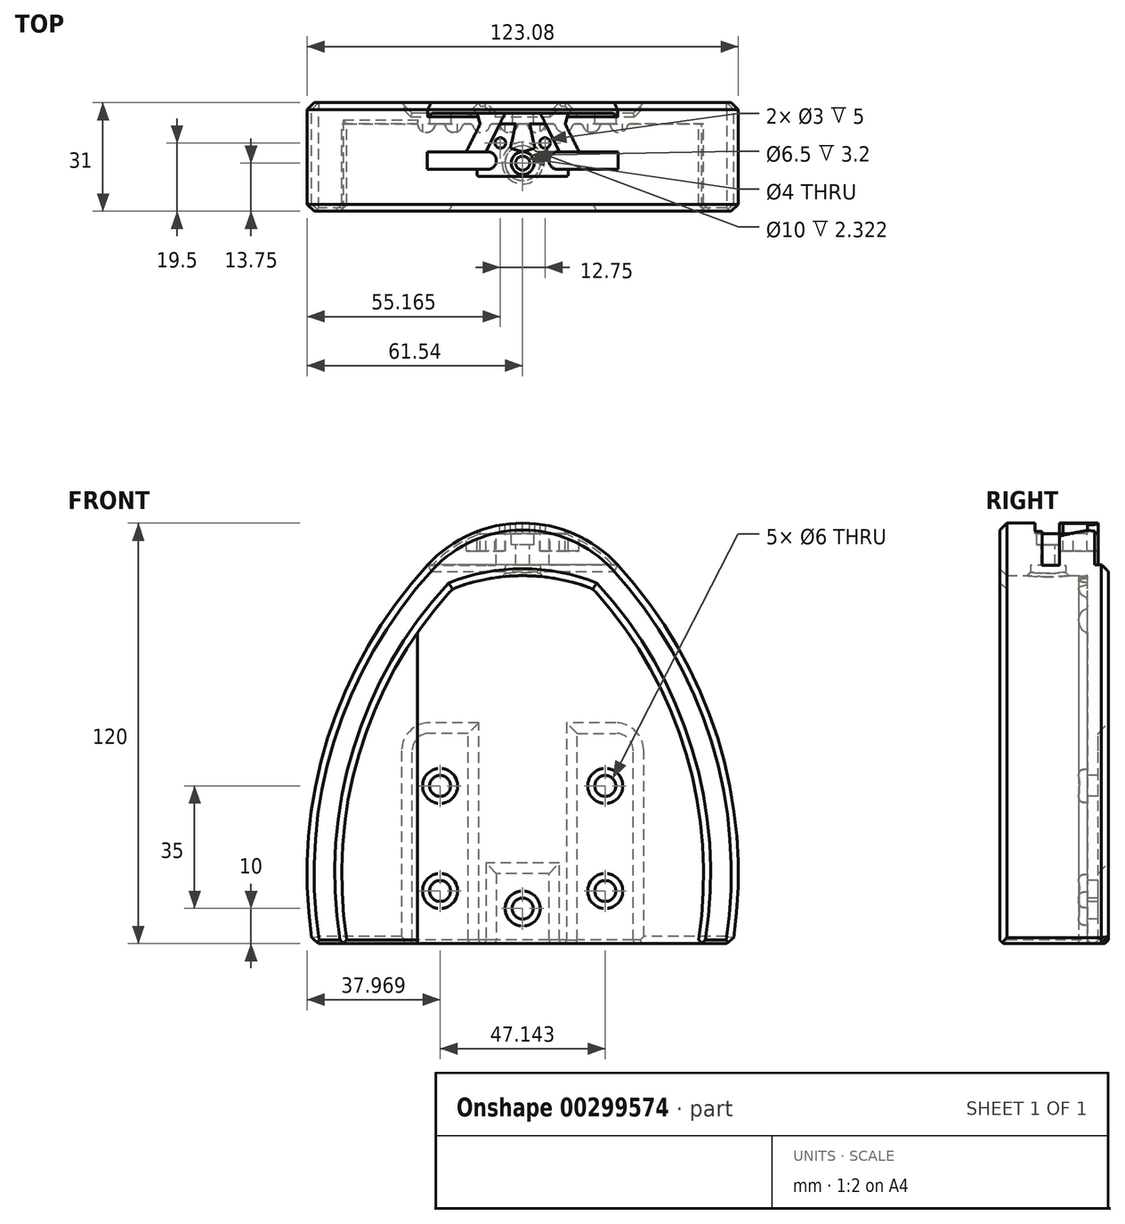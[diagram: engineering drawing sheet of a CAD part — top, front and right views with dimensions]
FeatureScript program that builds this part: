
annotation { "Feature Type Name" : "Feature", "Feature Type Description" : "" }
export const myFeature = defineFeature(function(context is Context, id is Id, definition is map)
    precondition{}
    {
        {
            assignVariable(context, id + "F0", {"name" : "LHeel", "anyValue" : 120 * mm});
        }
        {
            assignVariable(context, id + "F1", {"name" : "THeel", "anyValue" : 15 * mm});
        }
        {
            var Q0;
            Q0=qCreatedBy(makeId("Front.planeOp"),FACE);
            var sketch = newSketch(context, id + "F2", { "sketchPlane" : qUnion([Q0])});
            skArc(sketch, "E0", {"start": v(0, 120) * mm, "mid": v(-14.77, 116.9) * mm, "end": v(-27.05, 108.16) * mm});
            skArc(sketch, "E1", {"start": v(-27.05, 108.16) * mm, "mid": v(-55.9, 57.85) * mm, "end": v(-60, 0) * mm});
            skLineSegment(sketch, "E2", {"start": v(-60, 0) * mm, "end": v(0, 0) * mm});
            skArc(sketch, "E3.MirrorCS", {"start": v(0, 120) * mm, "mid": v(14.77, 116.9) * mm, "end": v(27.05, 108.16) * mm});
            skArc(sketch, "E4.MirrorCS", {"start": v(27.05, 108.16) * mm, "mid": v(55.9, 57.85) * mm, "end": v(60, 0) * mm});
            skLineSegment(sketch, "E5.MirrorCS", {"start": v(60, 0) * mm, "end": v(0, 0) * mm});
            skSolve(sketch);
        }
        {
            var Q0;
            Q0=makeQuery(id+"F2.imprint","IMPRINT",FACE,{"disambiguationData":[TD([[makeQuery(id+"F2.imprint","IMPRINT",EDGE,{"derivedFrom":sQuery(id+"F2.wireOp",EDGE,"E0")}),1.0]])]});
            extrude(context, id + "F3", {"entities" : qUnion([Q0]), "depth" : 3 * mm});
        }
        {
            var Q0;
            Q0=makeQuery(id+"F3.opExtrude","CAP_FACE",FACE,{"disambiguationData":[OSD([sQuery(id+"F2.wireOp",EDGE,"E0"),sQuery(id+"F2.wireOp",EDGE,"E1"),sQuery(id+"F2.wireOp",EDGE,"E2"),sQuery(id+"F2.wireOp",EDGE,"E3.MirrorCS"),sQuery(id+"F2.wireOp",EDGE,"E4.MirrorCS"),sQuery(id+"F2.wireOp",EDGE,"E5.MirrorCS")])],"isStart":false});
            var sketch = newSketch(context, id + "F4", { "sketchPlane" : qUnion([Q0])});
            skArc(sketch, "E6", {"start": v(0, 120) * mm, "mid": v(-14.77, 116.9) * mm, "end": v(-27.05, 108.16) * mm});
            skArc(sketch, "E7", {"start": v(-27.05, 108.16) * mm, "mid": v(-55.9, 57.85) * mm, "end": v(-60, 0) * mm});
            skArc(sketch, "E8", {"start": v(-20.01, 101.23) * mm, "mid": v(-46.72, 54.09) * mm, "end": v(-50, 0) * mm});
            skLineSegment(sketch, "E9", {"start": v(-60, 0) * mm, "end": v(-50, 0) * mm});
            skArc(sketch, "E10.MirrorCS", {"start": v(20.01, 101.23) * mm, "mid": v(46.72, 54.09) * mm, "end": v(50, 0) * mm});
            skLineSegment(sketch, "E11.MirrorCS", {"start": v(60, 0) * mm, "end": v(50, 0) * mm});
            skArc(sketch, "E12.MirrorCS", {"start": v(27.05, 108.16) * mm, "mid": v(55.9, 57.85) * mm, "end": v(60, 0) * mm});
            skArc(sketch, "E13.MirrorCS", {"start": v(0, 120) * mm, "mid": v(14.77, 116.9) * mm, "end": v(27.05, 108.16) * mm});
            skArc(sketch, "E14", {"start": v(20.01, 101.23) * mm, "mid": v(0, 105) * mm, "end": v(-20.01, 101.23) * mm});
            skPoint(sketch, "E15", {"position": v(0, 105) * mm});
            skSolve(sketch);
        }
        {
            var Q0;
            Q0 = qSketchRegion(id + "F4", true);
            extrude(context, id + "F5", {"entities" : qUnion([Q0]), "operationType" : NewBodyOperationType.ADD, "depth" : 25 * mm});
        }
        {
            var Q0;
            Q0=makeQuery(id+"F3.opExtrude","SWEPT_FACE",FACE,{"disambiguationData":[OSD([sQuery(id+"F2.wireOp",EDGE,"E2"),sQuery(id+"F2.wireOp",EDGE,"E5.MirrorCS")])]});
            var sketch = newSketch(context, id + "F6", { "sketchPlane" : qUnion([Q0])});
            skArc(sketch, "E16", {"start": v(-25, 3) * mm, "mid": v(-27.5, 5.5) * mm, "end": v(-30, 3) * mm});
            skLineSegment(sketch, "E17", {"start": v(-30, 3) * mm, "end": v(-25, 3) * mm});
            skArc(sketch, "E18.1.0.0", {"start": v(-17.14, 3) * mm, "mid": v(-19.64, 5.5) * mm, "end": v(-22.14, 3) * mm});
            skArc(sketch, "E18.2.0.0", {"start": v(-9.29, 3) * mm, "mid": v(-11.79, 5.5) * mm, "end": v(-14.29, 3) * mm});
            skArc(sketch, "E18.3.0.0", {"start": v(-1.43, 3) * mm, "mid": v(-3.93, 5.5) * mm, "end": v(-6.43, 3) * mm});
            skArc(sketch, "E18.4.0.0", {"start": v(6.43, 3) * mm, "mid": v(3.93, 5.5) * mm, "end": v(1.43, 3) * mm});
            skArc(sketch, "E18.5.0.0", {"start": v(14.29, 3) * mm, "mid": v(11.79, 5.5) * mm, "end": v(9.29, 3) * mm});
            skArc(sketch, "E18.6.0.0", {"start": v(22.14, 3) * mm, "mid": v(19.64, 5.5) * mm, "end": v(17.14, 3) * mm});
            skArc(sketch, "E18.7.0.0", {"start": v(30, 3) * mm, "mid": v(27.5, 5.5) * mm, "end": v(25, 3) * mm});
            skLineSegment(sketch, "E18.direction1", {"start": v(-30, 3) * mm, "end": v(-22.14, 3) * mm, "construction": true});
            skSolve(sketch);
        }
        {
            var Q0;
            Q0 = qSketchRegion(id + "F6", true);
            var Q1;
            {var subQ0=sQuery(id+"F6.wireOp",EDGE,"E18.1.0.0");Q1=makeQuery(id+"F6.imprint","IMPRINT",FACE,{"disambiguationData":[TD([[makeQuery(id+"F6.imprint","IMPRINT",EDGE,{"derivedFrom":subQ0}),1.0]])]});}
            var Q2;
            {var subQ0=sQuery(id+"F6.wireOp",EDGE,"E18.2.0.0");Q2=makeQuery(id+"F6.imprint","IMPRINT",FACE,{"disambiguationData":[TD([[makeQuery(id+"F6.imprint","IMPRINT",EDGE,{"derivedFrom":subQ0}),1.0]])]});}
            var Q3;
            {var subQ0=sQuery(id+"F6.wireOp",EDGE,"E18.3.0.0");Q3=makeQuery(id+"F6.imprint","IMPRINT",FACE,{"disambiguationData":[TD([[makeQuery(id+"F6.imprint","IMPRINT",EDGE,{"derivedFrom":subQ0}),1.0]])]});}
            var Q4;
            {var subQ0=sQuery(id+"F6.wireOp",EDGE,"E18.4.0.0");Q4=makeQuery(id+"F6.imprint","IMPRINT",FACE,{"disambiguationData":[TD([[makeQuery(id+"F6.imprint","IMPRINT",EDGE,{"derivedFrom":subQ0}),1.0]])]});}
            var Q5;
            {var subQ0=sQuery(id+"F6.wireOp",EDGE,"E18.5.0.0");Q5=makeQuery(id+"F6.imprint","IMPRINT",FACE,{"disambiguationData":[TD([[makeQuery(id+"F6.imprint","IMPRINT",EDGE,{"derivedFrom":subQ0}),1.0]])]});}
            var Q6;
            {var subQ0=sQuery(id+"F6.wireOp",EDGE,"E18.6.0.0");Q6=makeQuery(id+"F6.imprint","IMPRINT",FACE,{"disambiguationData":[TD([[makeQuery(id+"F6.imprint","IMPRINT",EDGE,{"derivedFrom":subQ0}),1.0]])]});}
            var Q7;
            {var subQ0=sQuery(id+"F6.wireOp",EDGE,"E18.7.0.0");Q7=makeQuery(id+"F6.imprint","IMPRINT",FACE,{"disambiguationData":[TD([[makeQuery(id+"F6.imprint","IMPRINT",EDGE,{"derivedFrom":subQ0}),1.0]])]});}
            var Q8;
            {var subQ0=sQuery(id+"F6.wireOp",EDGE,"E18.8.0.0");Q8=makeQuery(id+"F6.imprint","IMPRINT",FACE,{"disambiguationData":[TD([[makeQuery(id+"F6.imprint","IMPRINT",EDGE,{"derivedFrom":subQ0}),1.0]])]});}
            var Q9;
            {var subQ0=sQuery(id+"F6.wireOp",EDGE,"E18.9.0.0");Q9=makeQuery(id+"F6.imprint","IMPRINT",FACE,{"disambiguationData":[TD([[makeQuery(id+"F6.imprint","IMPRINT",EDGE,{"derivedFrom":subQ0}),1.0]])]});}
            extrude(context, id + "F7", {"entities" : qUnion([Q0, Q1, Q2, Q3, Q4, Q5, Q6, Q7, Q8, Q9]), "operationType" : NewBodyOperationType.ADD, "endBound" : BoundingType.UP_TO_NEXT, "oppositeDirection" : true, "depth" : 25 * mm});
        }
        {
            var Q0;
            {var subQ0=sQuery(id+"F6.wireOp",EDGE,"E17");var subQ1=sQuery(id+"F6.wireOp",EDGE,"E16");var subQ2=sQuery(id+"F2.wireOp",EDGE,"E5.MirrorCS");var subQ3=sQuery(id+"F2.wireOp",EDGE,"E2");Q0=makeQuery(id+"F7.opExtrude","SWEPT_EDGE",EDGE,{"disambiguationData":[OSD([subQ3,subQ2,subQ1,subQ0]),TDD([makeQuery(id+"F6.imprint","INTERSECT",VERTEX,{"disambiguationData":[OD(0.0)],"derivedFrom":[makeQuery(id+"F3.opExtrude","CAP_EDGE",EDGE,{"disambiguationData":[OSD([subQ3,subQ2])],"isStart":false}),subQ1,subQ0]})])]});}
            var Q1;
            {var subQ0=sQuery(id+"F6.wireOp",EDGE,"E18.1.0.0");var subQ1=sQuery(id+"F2.wireOp",EDGE,"E5.MirrorCS");var subQ2=sQuery(id+"F2.wireOp",EDGE,"E2");Q1=makeQuery(id+"F7.opExtrude","SWEPT_EDGE",EDGE,{"disambiguationData":[OSD([subQ2,subQ1,subQ0]),TDD([makeQuery(id+"F6.imprint","INTERSECT",VERTEX,{"disambiguationData":[OD(0.0)],"derivedFrom":[makeQuery(id+"F3.opExtrude","CAP_EDGE",EDGE,{"disambiguationData":[OSD([subQ2,subQ1])],"isStart":false}),subQ0]})])]});}
            var Q2;
            {var subQ0=sQuery(id+"F6.wireOp",EDGE,"E18.2.0.0");var subQ1=sQuery(id+"F2.wireOp",EDGE,"E5.MirrorCS");var subQ2=sQuery(id+"F2.wireOp",EDGE,"E2");Q2=makeQuery(id+"F7.opExtrude","SWEPT_EDGE",EDGE,{"disambiguationData":[OSD([subQ2,subQ1,subQ0]),TDD([makeQuery(id+"F6.imprint","INTERSECT",VERTEX,{"disambiguationData":[OD(0.0)],"derivedFrom":[makeQuery(id+"F3.opExtrude","CAP_EDGE",EDGE,{"disambiguationData":[OSD([subQ2,subQ1])],"isStart":false}),subQ0]})])]});}
            var Q3;
            {var subQ0=sQuery(id+"F6.wireOp",EDGE,"E18.3.0.0");var subQ1=sQuery(id+"F2.wireOp",EDGE,"E5.MirrorCS");var subQ2=sQuery(id+"F2.wireOp",EDGE,"E2");Q3=makeQuery(id+"F7.opExtrude","SWEPT_EDGE",EDGE,{"disambiguationData":[OSD([subQ2,subQ1,subQ0]),TDD([makeQuery(id+"F6.imprint","INTERSECT",VERTEX,{"disambiguationData":[OD(0.0)],"derivedFrom":[makeQuery(id+"F3.opExtrude","CAP_EDGE",EDGE,{"disambiguationData":[OSD([subQ2,subQ1])],"isStart":false}),subQ0]})])]});}
            var Q4;
            {var subQ0=sQuery(id+"F6.wireOp",EDGE,"E18.4.0.0");var subQ1=sQuery(id+"F2.wireOp",EDGE,"E5.MirrorCS");var subQ2=sQuery(id+"F2.wireOp",EDGE,"E2");Q4=makeQuery(id+"F7.opExtrude","SWEPT_EDGE",EDGE,{"disambiguationData":[OSD([subQ2,subQ1,subQ0]),TDD([makeQuery(id+"F6.imprint","INTERSECT",VERTEX,{"disambiguationData":[OD(0.0)],"derivedFrom":[makeQuery(id+"F3.opExtrude","CAP_EDGE",EDGE,{"disambiguationData":[OSD([subQ2,subQ1])],"isStart":false}),subQ0]})])]});}
            var Q5;
            {var subQ0=sQuery(id+"F6.wireOp",EDGE,"E18.5.0.0");var subQ1=sQuery(id+"F2.wireOp",EDGE,"E5.MirrorCS");var subQ2=sQuery(id+"F2.wireOp",EDGE,"E2");Q5=makeQuery(id+"F7.opExtrude","SWEPT_EDGE",EDGE,{"disambiguationData":[OSD([subQ2,subQ1,subQ0]),TDD([makeQuery(id+"F6.imprint","INTERSECT",VERTEX,{"disambiguationData":[OD(0.0)],"derivedFrom":[makeQuery(id+"F3.opExtrude","CAP_EDGE",EDGE,{"disambiguationData":[OSD([subQ2,subQ1])],"isStart":false}),subQ0]})])]});}
            var Q6;
            {var subQ0=sQuery(id+"F6.wireOp",EDGE,"E18.6.0.0");var subQ1=sQuery(id+"F2.wireOp",EDGE,"E5.MirrorCS");var subQ2=sQuery(id+"F2.wireOp",EDGE,"E2");Q6=makeQuery(id+"F7.opExtrude","SWEPT_EDGE",EDGE,{"disambiguationData":[OSD([subQ2,subQ1,subQ0]),TDD([makeQuery(id+"F6.imprint","INTERSECT",VERTEX,{"disambiguationData":[OD(0.0)],"derivedFrom":[makeQuery(id+"F3.opExtrude","CAP_EDGE",EDGE,{"disambiguationData":[OSD([subQ2,subQ1])],"isStart":false}),subQ0]})])]});}
            var Q7;
            {var subQ0=sQuery(id+"F6.wireOp",EDGE,"E18.7.0.0");var subQ1=sQuery(id+"F2.wireOp",EDGE,"E5.MirrorCS");var subQ2=sQuery(id+"F2.wireOp",EDGE,"E2");Q7=makeQuery(id+"F7.opExtrude","SWEPT_EDGE",EDGE,{"disambiguationData":[OSD([subQ2,subQ1,subQ0]),TDD([makeQuery(id+"F6.imprint","INTERSECT",VERTEX,{"disambiguationData":[OD(0.0)],"derivedFrom":[makeQuery(id+"F3.opExtrude","CAP_EDGE",EDGE,{"disambiguationData":[OSD([subQ2,subQ1])],"isStart":false}),subQ0]})])]});}
            var Q8;
            {var subQ0=sQuery(id+"F6.wireOp",EDGE,"E18.8.0.0");var subQ1=sQuery(id+"F2.wireOp",EDGE,"E5.MirrorCS");var subQ2=sQuery(id+"F2.wireOp",EDGE,"E2");Q8=makeQuery(id+"F7.opExtrude","SWEPT_EDGE",EDGE,{"disambiguationData":[OSD([subQ2,subQ1,subQ0]),TDD([makeQuery(id+"F6.imprint","INTERSECT",VERTEX,{"disambiguationData":[OD(0.0)],"derivedFrom":[makeQuery(id+"F3.opExtrude","CAP_EDGE",EDGE,{"disambiguationData":[OSD([subQ2,subQ1])],"isStart":false}),subQ0]})])]});}
            var Q9;
            {var subQ0=sQuery(id+"F6.wireOp",EDGE,"E18.9.0.0");var subQ1=sQuery(id+"F2.wireOp",EDGE,"E5.MirrorCS");var subQ2=sQuery(id+"F2.wireOp",EDGE,"E2");Q9=makeQuery(id+"F7.opExtrude","SWEPT_EDGE",EDGE,{"disambiguationData":[OSD([subQ2,subQ1,subQ0]),TDD([makeQuery(id+"F6.imprint","INTERSECT",VERTEX,{"disambiguationData":[OD(0.0)],"derivedFrom":[makeQuery(id+"F3.opExtrude","CAP_EDGE",EDGE,{"disambiguationData":[OSD([subQ2,subQ1])],"isStart":false}),subQ0]})])]});}
            var Q10;
            {var subQ0=sQuery(id+"F6.wireOp",EDGE,"E18.9.0.0");var subQ1=sQuery(id+"F2.wireOp",EDGE,"E5.MirrorCS");var subQ2=sQuery(id+"F2.wireOp",EDGE,"E2");Q10=makeQuery(id+"F7.opExtrude","SWEPT_EDGE",EDGE,{"disambiguationData":[OSD([subQ2,subQ1,subQ0]),TDD([makeQuery(id+"F6.imprint","INTERSECT",VERTEX,{"disambiguationData":[OD(1.0)],"derivedFrom":[makeQuery(id+"F3.opExtrude","CAP_EDGE",EDGE,{"disambiguationData":[OSD([subQ2,subQ1])],"isStart":false}),subQ0]})])]});}
            var Q11;
            {var subQ0=sQuery(id+"F6.wireOp",EDGE,"E18.8.0.0");var subQ1=sQuery(id+"F2.wireOp",EDGE,"E5.MirrorCS");var subQ2=sQuery(id+"F2.wireOp",EDGE,"E2");Q11=makeQuery(id+"F7.opExtrude","SWEPT_EDGE",EDGE,{"disambiguationData":[OSD([subQ2,subQ1,subQ0]),TDD([makeQuery(id+"F6.imprint","INTERSECT",VERTEX,{"disambiguationData":[OD(1.0)],"derivedFrom":[makeQuery(id+"F3.opExtrude","CAP_EDGE",EDGE,{"disambiguationData":[OSD([subQ2,subQ1])],"isStart":false}),subQ0]})])]});}
            var Q12;
            {var subQ0=sQuery(id+"F6.wireOp",EDGE,"E18.7.0.0");var subQ1=sQuery(id+"F2.wireOp",EDGE,"E5.MirrorCS");var subQ2=sQuery(id+"F2.wireOp",EDGE,"E2");Q12=makeQuery(id+"F7.opExtrude","SWEPT_EDGE",EDGE,{"disambiguationData":[OSD([subQ2,subQ1,subQ0]),TDD([makeQuery(id+"F6.imprint","INTERSECT",VERTEX,{"disambiguationData":[OD(1.0)],"derivedFrom":[makeQuery(id+"F3.opExtrude","CAP_EDGE",EDGE,{"disambiguationData":[OSD([subQ2,subQ1])],"isStart":false}),subQ0]})])]});}
            var Q13;
            {var subQ0=sQuery(id+"F6.wireOp",EDGE,"E18.6.0.0");var subQ1=sQuery(id+"F2.wireOp",EDGE,"E5.MirrorCS");var subQ2=sQuery(id+"F2.wireOp",EDGE,"E2");Q13=makeQuery(id+"F7.opExtrude","SWEPT_EDGE",EDGE,{"disambiguationData":[OSD([subQ2,subQ1,subQ0]),TDD([makeQuery(id+"F6.imprint","INTERSECT",VERTEX,{"disambiguationData":[OD(1.0)],"derivedFrom":[makeQuery(id+"F3.opExtrude","CAP_EDGE",EDGE,{"disambiguationData":[OSD([subQ2,subQ1])],"isStart":false}),subQ0]})])]});}
            var Q14;
            {var subQ0=sQuery(id+"F6.wireOp",EDGE,"E18.5.0.0");var subQ1=sQuery(id+"F2.wireOp",EDGE,"E5.MirrorCS");var subQ2=sQuery(id+"F2.wireOp",EDGE,"E2");Q14=makeQuery(id+"F7.opExtrude","SWEPT_EDGE",EDGE,{"disambiguationData":[OSD([subQ2,subQ1,subQ0]),TDD([makeQuery(id+"F6.imprint","INTERSECT",VERTEX,{"disambiguationData":[OD(1.0)],"derivedFrom":[makeQuery(id+"F3.opExtrude","CAP_EDGE",EDGE,{"disambiguationData":[OSD([subQ2,subQ1])],"isStart":false}),subQ0]})])]});}
            var Q15;
            {var subQ0=sQuery(id+"F6.wireOp",EDGE,"E18.4.0.0");var subQ1=sQuery(id+"F2.wireOp",EDGE,"E5.MirrorCS");var subQ2=sQuery(id+"F2.wireOp",EDGE,"E2");Q15=makeQuery(id+"F7.opExtrude","SWEPT_EDGE",EDGE,{"disambiguationData":[OSD([subQ2,subQ1,subQ0]),TDD([makeQuery(id+"F6.imprint","INTERSECT",VERTEX,{"disambiguationData":[OD(1.0)],"derivedFrom":[makeQuery(id+"F3.opExtrude","CAP_EDGE",EDGE,{"disambiguationData":[OSD([subQ2,subQ1])],"isStart":false}),subQ0]})])]});}
            var Q16;
            {var subQ0=sQuery(id+"F6.wireOp",EDGE,"E18.3.0.0");var subQ1=sQuery(id+"F2.wireOp",EDGE,"E5.MirrorCS");var subQ2=sQuery(id+"F2.wireOp",EDGE,"E2");Q16=makeQuery(id+"F7.opExtrude","SWEPT_EDGE",EDGE,{"disambiguationData":[OSD([subQ2,subQ1,subQ0]),TDD([makeQuery(id+"F6.imprint","INTERSECT",VERTEX,{"disambiguationData":[OD(1.0)],"derivedFrom":[makeQuery(id+"F3.opExtrude","CAP_EDGE",EDGE,{"disambiguationData":[OSD([subQ2,subQ1])],"isStart":false}),subQ0]})])]});}
            var Q17;
            {var subQ0=sQuery(id+"F6.wireOp",EDGE,"E18.2.0.0");var subQ1=sQuery(id+"F2.wireOp",EDGE,"E5.MirrorCS");var subQ2=sQuery(id+"F2.wireOp",EDGE,"E2");Q17=makeQuery(id+"F7.opExtrude","SWEPT_EDGE",EDGE,{"disambiguationData":[OSD([subQ2,subQ1,subQ0]),TDD([makeQuery(id+"F6.imprint","INTERSECT",VERTEX,{"disambiguationData":[OD(1.0)],"derivedFrom":[makeQuery(id+"F3.opExtrude","CAP_EDGE",EDGE,{"disambiguationData":[OSD([subQ2,subQ1])],"isStart":false}),subQ0]})])]});}
            var Q18;
            {var subQ0=sQuery(id+"F6.wireOp",EDGE,"E18.1.0.0");var subQ1=sQuery(id+"F2.wireOp",EDGE,"E5.MirrorCS");var subQ2=sQuery(id+"F2.wireOp",EDGE,"E2");Q18=makeQuery(id+"F7.opExtrude","SWEPT_EDGE",EDGE,{"disambiguationData":[OSD([subQ2,subQ1,subQ0]),TDD([makeQuery(id+"F6.imprint","INTERSECT",VERTEX,{"disambiguationData":[OD(1.0)],"derivedFrom":[makeQuery(id+"F3.opExtrude","CAP_EDGE",EDGE,{"disambiguationData":[OSD([subQ2,subQ1])],"isStart":false}),subQ0]})])]});}
            var Q19;
            {var subQ0=sQuery(id+"F6.wireOp",EDGE,"E17");var subQ1=sQuery(id+"F6.wireOp",EDGE,"E16");var subQ2=sQuery(id+"F2.wireOp",EDGE,"E5.MirrorCS");var subQ3=sQuery(id+"F2.wireOp",EDGE,"E2");Q19=makeQuery(id+"F7.opExtrude","SWEPT_EDGE",EDGE,{"disambiguationData":[OSD([subQ3,subQ2,subQ1,subQ0]),TDD([makeQuery(id+"F6.imprint","INTERSECT",VERTEX,{"disambiguationData":[OD(1.0)],"derivedFrom":[makeQuery(id+"F3.opExtrude","CAP_EDGE",EDGE,{"disambiguationData":[OSD([subQ3,subQ2])],"isStart":false}),subQ1,subQ0]})])]});}
            fillet(context, id + "F8", {"entities" : qUnion([Q0, Q1, Q2, Q3, Q4, Q5, Q6, Q7, Q8, Q9, Q10, Q11, Q12, Q13, Q14, Q15, Q16, Q17, Q18, Q19]), "radius" : 1 * mm, "tangentPropagation" : true, "allowEdgeOverflow" : false});
        }
        {
            var Q0;
            Q0=qCreatedBy(makeId("Top.planeOp"),FACE);
            cPlane(context, id + "F9", {"entities" : qUnion([Q0]), "cplaneType" : CPlaneType.OFFSET, "offset" : getVariable(context, 'LHeel'), "width" : 150 * mm, "height" : 150 * mm});
        }
        {
            var Q0;
            Q0=qCreatedBy(id+"F9.planeOp",FACE);
            var sketch = newSketch(context, id + "F10", { "sketchPlane" : qUnion([Q0])});
            skLineSegment(sketch, "E19", {"start": v(35, -11) * mm, "end": v(10, -11) * mm});
            skLineSegment(sketch, "E20", {"start": v(10, -16) * mm, "end": v(35, -16) * mm});
            skLineSegment(sketch, "E21", {"start": v(35, -16) * mm, "end": v(35, -11) * mm});
            skArc(sketch, "E22", {"start": v(10, -11) * mm, "mid": v(7.5, -13.5) * mm, "end": v(10, -16) * mm});
            skLineSegment(sketch, "E23.MirrorCS", {"start": v(-35, -11) * mm, "end": v(-10, -11) * mm});
            skLineSegment(sketch, "E24.MirrorCS", {"start": v(-35, -16) * mm, "end": v(-35, -11) * mm});
            skLineSegment(sketch, "E25.MirrorCS", {"start": v(-10, -16) * mm, "end": v(-35, -16) * mm});
            skArc(sketch, "E26.MirrorCS", {"start": v(-10, -11) * mm, "mid": v(-7.5, -13.5) * mm, "end": v(-10, -16) * mm});
            skSolve(sketch);
        }
        {
            var Q0;
            Q0 = qSketchRegion(id + "F10", true);
            extrude(context, id + "F11", {"entities" : qUnion([Q0]), "operationType" : NewBodyOperationType.REMOVE, "oppositeDirection" : true, "depth" : 12 * mm});
        }
        {
            var Q0;
            Q0=qCreatedBy(id+"F9.planeOp",FACE);
            var sketch = newSketch(context, id + "F12", { "sketchPlane" : qUnion([Q0])});
            skLineSegment(sketch, "E27", {"start": v(-5, 0) * mm, "end": v(-10.5, -11) * mm});
            skLineSegment(sketch, "E28", {"start": v(-10.5, -11) * mm, "end": v(-16.1, -11) * mm});
            skLineSegment(sketch, "E29", {"start": v(-16.1, -11) * mm, "end": v(-12.16, -3.14) * mm});
            skLineSegment(sketch, "E30", {"start": v(-12.16, -3.14) * mm, "end": v(-13, 0) * mm});
            skLineSegment(sketch, "E31", {"start": v(-13, 0) * mm, "end": v(-5, 0) * mm});
            skLineSegment(sketch, "E32.MirrorCS", {"start": v(12.16, -3.14) * mm, "end": v(13, 0) * mm});
            skLineSegment(sketch, "E33.MirrorCS", {"start": v(13, 0) * mm, "end": v(5, 0) * mm});
            skLineSegment(sketch, "E34.MirrorCS", {"start": v(10.5, -11) * mm, "end": v(16.1, -11) * mm});
            skLineSegment(sketch, "E35.MirrorCS", {"start": v(16.1, -11) * mm, "end": v(12.16, -3.14) * mm});
            skLineSegment(sketch, "E36.MirrorCS", {"start": v(5, 0) * mm, "end": v(10.5, -11) * mm});
            skSolve(sketch);
        }
        {
            var Q0;
            Q0 = qSketchRegion(id + "F12", true);
            extrude(context, id + "F13", {"entities" : qUnion([Q0]), "operationType" : NewBodyOperationType.REMOVE, "oppositeDirection" : true, "depth" : 8 * mm});
        }
        {
            var Q0;
            Q0=qCreatedBy(id+"F9.planeOp",FACE);
            var sketch = newSketch(context, id + "F14", { "sketchPlane" : qUnion([Q0])});
            skLineSegment(sketch, "E37", {"start": v(-6.5, -3) * mm, "end": v(-2, -3) * mm});
            skLineSegment(sketch, "E38", {"start": v(-2, -3) * mm, "end": v(-3.5, -10) * mm});
            skLineSegment(sketch, "E39", {"start": v(-3.5, -10) * mm, "end": v(0, -11) * mm});
            skLineSegment(sketch, "E40", {"start": v(-6.5, -3) * mm, "end": v(-10.5, -11) * mm});
            skLineSegment(sketch, "E41", {"start": v(-13, -16) * mm, "end": v(-13, -18) * mm});
            skLineSegment(sketch, "E42", {"start": v(-13, -18) * mm, "end": v(0, -18) * mm});
            skLineSegment(sketch, "E43", {"start": v(-13, -16) * mm, "end": v(-10, -16) * mm});
            skLineSegment(sketch, "E44.MirrorCS", {"start": v(6.5, -3) * mm, "end": v(2, -3) * mm});
            skLineSegment(sketch, "E45.MirrorCS", {"start": v(6.5, -3) * mm, "end": v(10.5, -11) * mm});
            skLineSegment(sketch, "E46.MirrorCS", {"start": v(3.5, -10) * mm, "end": v(0, -11) * mm});
            skLineSegment(sketch, "E47.MirrorCS", {"start": v(2, -3) * mm, "end": v(3.5, -10) * mm});
            skLineSegment(sketch, "E48.MirrorCS", {"start": v(13, -16) * mm, "end": v(13, -18) * mm});
            skLineSegment(sketch, "E49.MirrorCS", {"start": v(13, -18) * mm, "end": v(0, -18) * mm});
            skLineSegment(sketch, "E50.MirrorCS", {"start": v(13, -16) * mm, "end": v(10, -16) * mm});
            skLineSegment(sketch, "E51", {"start": v(-10.5, -11) * mm, "end": v(-10, -11) * mm});
            skArc(sketch, "E52", {"start": v(-10, -16) * mm, "mid": v(-7.5, -13.5) * mm, "end": v(-10, -11) * mm});
            skLineSegment(sketch, "E53.MirrorCS", {"start": v(10.5, -11) * mm, "end": v(10, -11) * mm});
            skArc(sketch, "E54.MirrorCS", {"start": v(10, -16) * mm, "mid": v(7.5, -13.5) * mm, "end": v(10, -11) * mm});
            skSolve(sketch);
        }
        {
            var Q0;
            Q0 = qSketchRegion(id + "F14", true);
            extrude(context, id + "F15", {"entities" : qUnion([Q0]), "operationType" : NewBodyOperationType.REMOVE, "oppositeDirection" : true, "depth" : 3 * mm});
        }
        {
            var Q0;
            Q0=makeQuery(id+"F15.boolean.opBoolean","COPY",EDGE,{"derivedFrom":makeQuery(id+"F15.opExtrude","SWEPT_EDGE",EDGE,{"disambiguationData":[OSD([sQuery(id+"F14.wireOp",EDGE,"E48.MirrorCS"),sQuery(id+"F14.wireOp",EDGE,"E49.MirrorCS")])]})});
            var Q1;
            Q1=makeQuery(id+"F15.boolean.opBoolean","COPY",EDGE,{"derivedFrom":makeQuery(id+"F15.opExtrude","SWEPT_EDGE",EDGE,{"disambiguationData":[OSD([sQuery(id+"F14.wireOp",EDGE,"E41"),sQuery(id+"F14.wireOp",EDGE,"E42")])]})});
            fillet(context, id + "F16", {"entities" : qUnion([Q0, Q1]), "radius" : .5 * mm, "tangentPropagation" : true, "allowEdgeOverflow" : false});
        }
        {
            var Q0;
            Q0=makeQuery(id+"F15.boolean.opBoolean","COPY",FACE,{"derivedFrom":makeQuery(id+"F15.opExtrude","CAP_FACE",FACE,{"disambiguationData":[OSD([sQuery(id+"F14.wireOp",EDGE,"E37"),sQuery(id+"F14.wireOp",EDGE,"E38"),sQuery(id+"F14.wireOp",EDGE,"E39"),sQuery(id+"F14.wireOp",EDGE,"E40"),sQuery(id+"F14.wireOp",EDGE,"E41"),sQuery(id+"F14.wireOp",EDGE,"E42"),sQuery(id+"F14.wireOp",EDGE,"E43"),sQuery(id+"F14.wireOp",EDGE,"E44.MirrorCS"),sQuery(id+"F14.wireOp",EDGE,"E45.MirrorCS"),sQuery(id+"F14.wireOp",EDGE,"E46.MirrorCS"),sQuery(id+"F14.wireOp",EDGE,"E47.MirrorCS"),sQuery(id+"F14.wireOp",EDGE,"E48.MirrorCS"),sQuery(id+"F14.wireOp",EDGE,"E49.MirrorCS"),sQuery(id+"F14.wireOp",EDGE,"E50.MirrorCS"),sQuery(id+"F14.wireOp",EDGE,"E51"),sQuery(id+"F14.wireOp",EDGE,"E52"),sQuery(id+"F14.wireOp",EDGE,"E53.MirrorCS"),sQuery(id+"F14.wireOp",EDGE,"E54.MirrorCS")])],"isStart":false})});
            var sketch = newSketch(context, id + "F17", { "sketchPlane" : qUnion([Q0])});
            skCircle(sketch, "E55", {"center": v(0, -14.25) * mm, "radius": 3.25 * mm});
            skSolve(sketch);
        }
        {
            var Q0;
            Q0 = qSketchRegion(id + "F17", true);
            extrude(context, id + "F18", {"entities" : qUnion([Q0]), "operationType" : NewBodyOperationType.REMOVE, "oppositeDirection" : true, "depth" : 3.2 * mm});
        }
        {
            var Q0;
            Q0=makeQuery(id+"F15.boolean.opBoolean","COPY",FACE,{"derivedFrom":makeQuery(id+"F15.opExtrude","CAP_FACE",FACE,{"disambiguationData":[OSD([sQuery(id+"F14.wireOp",EDGE,"E37"),sQuery(id+"F14.wireOp",EDGE,"E38"),sQuery(id+"F14.wireOp",EDGE,"E39"),sQuery(id+"F14.wireOp",EDGE,"E40"),sQuery(id+"F14.wireOp",EDGE,"E41"),sQuery(id+"F14.wireOp",EDGE,"E42"),sQuery(id+"F14.wireOp",EDGE,"E43"),sQuery(id+"F14.wireOp",EDGE,"E44.MirrorCS"),sQuery(id+"F14.wireOp",EDGE,"E45.MirrorCS"),sQuery(id+"F14.wireOp",EDGE,"E46.MirrorCS"),sQuery(id+"F14.wireOp",EDGE,"E47.MirrorCS"),sQuery(id+"F14.wireOp",EDGE,"E48.MirrorCS"),sQuery(id+"F14.wireOp",EDGE,"E49.MirrorCS"),sQuery(id+"F14.wireOp",EDGE,"E50.MirrorCS"),sQuery(id+"F14.wireOp",EDGE,"E51"),sQuery(id+"F14.wireOp",EDGE,"E52"),sQuery(id+"F14.wireOp",EDGE,"E53.MirrorCS"),sQuery(id+"F14.wireOp",EDGE,"E54.MirrorCS")])],"isStart":false})});
            var sketch = newSketch(context, id + "F19", { "sketchPlane" : qUnion([Q0])});
            skCircle(sketch, "E56", {"center": v(6.38, -8.5) * mm, "radius": 1.5 * mm});
            skCircle(sketch, "E57.MirrorC", {"center": v(-6.38, -8.5) * mm, "radius": 1.5 * mm});
            skSolve(sketch);
        }
        {
            var Q0;
            Q0 = qSketchRegion(id + "F19", true);
            extrude(context, id + "F20", {"entities" : qUnion([Q0]), "operationType" : NewBodyOperationType.REMOVE, "oppositeDirection" : true, "depth" : 5 * mm});
        }
        {
            var Q0;
            Q0=makeQuery(id+"F15.boolean.opBoolean","COPY",FACE,{"derivedFrom":makeQuery(id+"F15.opExtrude","CAP_FACE",FACE,{"disambiguationData":[OSD([sQuery(id+"F14.wireOp",EDGE,"E37"),sQuery(id+"F14.wireOp",EDGE,"E38"),sQuery(id+"F14.wireOp",EDGE,"E39"),sQuery(id+"F14.wireOp",EDGE,"E40"),sQuery(id+"F14.wireOp",EDGE,"E41"),sQuery(id+"F14.wireOp",EDGE,"E42"),sQuery(id+"F14.wireOp",EDGE,"E43"),sQuery(id+"F14.wireOp",EDGE,"E44.MirrorCS"),sQuery(id+"F14.wireOp",EDGE,"E45.MirrorCS"),sQuery(id+"F14.wireOp",EDGE,"E46.MirrorCS"),sQuery(id+"F14.wireOp",EDGE,"E47.MirrorCS"),sQuery(id+"F14.wireOp",EDGE,"E48.MirrorCS"),sQuery(id+"F14.wireOp",EDGE,"E49.MirrorCS"),sQuery(id+"F14.wireOp",EDGE,"E50.MirrorCS"),sQuery(id+"F14.wireOp",EDGE,"E51"),sQuery(id+"F14.wireOp",EDGE,"E52"),sQuery(id+"F14.wireOp",EDGE,"E53.MirrorCS"),sQuery(id+"F14.wireOp",EDGE,"E54.MirrorCS")])],"isStart":false})});
            var sketch = newSketch(context, id + "F21", { "sketchPlane" : qUnion([Q0])});
            skCircle(sketch, "E58", {"center": v(0, -14.25) * mm, "radius": 2 * mm});
            skSolve(sketch);
        }
        {
            var Q0;
            Q0 = qSketchRegion(id + "F21", true);
            extrude(context, id + "F22", {"entities" : qUnion([Q0]), "operationType" : NewBodyOperationType.REMOVE, "oppositeDirection" : true, "depth" : 25 * mm});
        }
        {
            var Q0;
            Q0=qCreatedBy(makeId("Top.planeOp"),FACE);
            cPlane(context, id + "F23", {"entities" : qUnion([Q0]), "cplaneType" : CPlaneType.OFFSET, "offset" : getVariable(context, 'LHeel') - getVariable(context, 'THeel'), "width" : 150 * mm, "height" : 150 * mm});
        }
        {
            var Q0;
            Q0=qCreatedBy(id+"F23.planeOp",FACE);
            var sketch = newSketch(context, id + "F24", { "sketchPlane" : qUnion([Q0])});
            skCircle(sketch, "E59", {"center": v(0, -14.25) * mm, "radius": 2 * mm});
            skCircle(sketch, "E60", {"center": v(0, -14.25) * mm, "radius": 5 * mm});
            skSolve(sketch);
        }
        {
            var Q0;
            Q0 = qSketchRegion(id + "F24", true);
            extrude(context, id + "F25", {"entities" : qUnion([Q0]), "operationType" : NewBodyOperationType.REMOVE, "depth" : 3 * mm, "hasSecondDirection" : true, "secondDirectionOppositeDirection" : true, "secondDirectionDepth" : 25 * mm});
        }
        {
            var Q0;
            {var subQ0=sQuery(id+"F6.wireOp",EDGE,"E18.6.0.0");var subQ1=sQuery(id+"F2.wireOp",EDGE,"E5.MirrorCS");var subQ2=sQuery(id+"F2.wireOp",EDGE,"E2");var subQ3=makeQuery(id+"F7.opExtrude","CAP_FACE",FACE,{"disambiguationData":[OSD([subQ2,subQ1,subQ0])],"isStart":true});var subQ4=makeQuery(id+"F7.opExtrude","CAP_FACE",FACE,{"disambiguationData":[OSD([subQ2,subQ1,sQuery(id+"F6.wireOp",EDGE,"E18.4.0.0")])],"isStart":true});var subQ5=makeQuery(id+"F7.opExtrude","CAP_FACE",FACE,{"disambiguationData":[OSD([subQ2,subQ1,sQuery(id+"F6.wireOp",EDGE,"E18.3.0.0")])],"isStart":true});var subQ6=makeQuery(id+"F3.opExtrude","SWEPT_FACE",FACE,{"disambiguationData":[OSD([subQ2,subQ1])]});var subQ7=makeQuery(id+"F7.opExtrude","CAP_FACE",FACE,{"disambiguationData":[OSD([subQ2,subQ1,sQuery(id+"F6.wireOp",EDGE,"E18.2.0.0")])],"isStart":true});var subQ8=makeQuery(id+"F5.opExtrude","SWEPT_FACE",FACE,{"disambiguationData":[OSD([sQuery(id+"F4.wireOp",EDGE,"FZn0JHBI-A9Gq-jUhd-VDxp-ANsdCAXQZEyL"),sQuery(id+"F4.wireOp",EDGE,"94862bb9-d334-4f4f-86bf-2b5ff63ee9990.MirrorCS")])]});var subQ9=sQuery(id+"F6.wireOp",EDGE,"E18.7.0.0");var subQ10=makeQuery(id+"F7.opExtrude","SWEPT_FACE",FACE,{"disambiguationData":[OSD([subQ9])]});var subQ11=makeQuery(id+"F7.opExtrude","CAP_FACE",FACE,{"disambiguationData":[OSD([subQ2,subQ1,sQuery(id+"F6.wireOp",EDGE,"E18.1.0.0")])],"isStart":true});var subQ12=makeQuery(id+"F7.opExtrude","CAP_FACE",FACE,{"disambiguationData":[OSD([subQ2,subQ1,sQuery(id+"F6.wireOp",EDGE,"E18.5.0.0")])],"isStart":true});var subQ13=makeQuery(id+"F7.opExtrude","CAP_FACE",FACE,{"disambiguationData":[OSD([sQuery(id+"F6.wireOp",EDGE,"E16"),sQuery(id+"F6.wireOp",EDGE,"E17")])],"isStart":true});var subQ14=makeQuery(id+"F7.opExtrude","CAP_FACE",FACE,{"disambiguationData":[OSD([subQ2,subQ1,subQ9])],"isStart":true});var subQ15=sQuery(id+"F6.wireOp",EDGE,"E18.8.0.0");var subQ16=makeQuery(id+"F7.opExtrude","SWEPT_FACE",FACE,{"disambiguationData":[OSD([subQ15])]});var subQ17=makeQuery(id+"F7.opExtrude","CAP_FACE",FACE,{"disambiguationData":[OSD([subQ2,subQ1,subQ15])],"isStart":true});var subQ18=sQuery(id+"F6.wireOp",EDGE,"E18.9.0.0");var subQ19=makeQuery(id+"F7.opExtrude","CAP_FACE",FACE,{"disambiguationData":[OSD([subQ2,subQ1,subQ18])],"isStart":true});var subQ20=makeQuery(id+"F3.opExtrude","CAP_FACE",FACE,{"disambiguationData":[OSD([sQuery(id+"F2.wireOp",EDGE,"E0"),sQuery(id+"F2.wireOp",EDGE,"E1"),subQ2,sQuery(id+"F2.wireOp",EDGE,"E3.MirrorCS"),sQuery(id+"F2.wireOp",EDGE,"E4.MirrorCS"),subQ1])],"isStart":false});Q0=makeQuery(id+"FuolT4ABAihHTZn_1.boolean.opBoolean","MERGE",FACE,{"derivedFrom":[makeQuery(id+"F7.boolean.opBoolean","SPLIT",FACE,{"disambiguationData":[TD([subQ6,subQ8,makeQuery(id+"F5.opExtrude","SWEPT_FACE",FACE,{"disambiguationData":[OSD([sQuery(id+"F4.wireOp",EDGE,"E10.MirrorCS")])]}),subQ13,subQ11,subQ7,subQ5,subQ4,subQ12,subQ3,subQ14,subQ16,subQ17,makeQuery(id+"F7.opExtrude","SWEPT_FACE",FACE,{"disambiguationData":[OSD([subQ18])]}),subQ19])],"derivedFrom":subQ20}),makeQuery(id+"F7.boolean.opBoolean","SPLIT",FACE,{"disambiguationData":[TD([subQ6,subQ8,subQ13,subQ11,subQ7,subQ5,subQ4,subQ12,makeQuery(id+"F7.opExtrude","SWEPT_FACE",FACE,{"disambiguationData":[OSD([subQ0])]}),subQ3,subQ10,subQ14,subQ17,subQ19])],"derivedFrom":subQ20}),makeQuery(id+"F7.boolean.opBoolean","SPLIT",FACE,{"disambiguationData":[TD([subQ6,subQ8,subQ13,subQ11,subQ7,subQ5,subQ4,subQ12,subQ3,subQ10,subQ14,subQ16,subQ17,subQ19])],"derivedFrom":subQ20}),makeQuery(id+"FuolT4ABAihHTZn_1.opExtrude","SWEPT_FACE",FACE,{"disambiguationData":[OSD([sQuery(id+"FIxBE3dgotSAZQS_1.wireOp",EDGE,"DbaOr28i-rK8a-sUH4-Cgqk-jCIZV5dNe7y5.bottom")])]})]});}
            var sketch = newSketch(context, id + "F26", { "sketchPlane" : qUnion([Q0])});
            skCircle(sketch, "E61", {"center": v(-23.57, 45) * mm, "radius": 3 * mm});
            skCircle(sketch, "E62", {"center": v(-23.57, 15) * mm, "radius": 3 * mm});
            skCircle(sketch, "E63.MirrorC", {"center": v(23.57, 45) * mm, "radius": 3 * mm});
            skCircle(sketch, "E64.MirrorC", {"center": v(23.57, 15) * mm, "radius": 3 * mm});
            skPoint(sketch, "E65", {"position": v(-23.57, 0) * mm});
            skPoint(sketch, "E66", {"position": v(23.57, 0) * mm});
            skCircle(sketch, "E67", {"center": v(0, 10) * mm, "radius": 3 * mm});
            skPoint(sketch, "E68", {"position": v(0, 0) * mm});
            skSolve(sketch);
        }
        {
            var Q0;
            Q0 = qSketchRegion(id + "F26", true);
            extrude(context, id + "F27", {"entities" : qUnion([Q0]), "operationType" : NewBodyOperationType.REMOVE, "oppositeDirection" : true, "depth" : 25 * mm});
        }
        {
            var Q0;
            {var subQ0=sQuery(id+"F2.wireOp",EDGE,"E5.MirrorCS");var subQ1=sQuery(id+"F2.wireOp",EDGE,"E2");var subQ2=sQuery(id+"F6.wireOp",EDGE,"E16");var subQ3=sQuery(id+"F2.wireOp",EDGE,"E1");Q0=makeQuery(id+"F7.boolean.opBoolean","SPLIT",FACE,{"disambiguationData":[TD([makeQuery(id+"F3.opExtrude","SWEPT_FACE",FACE,{"disambiguationData":[OSD([subQ3])]}),makeQuery(id+"F3.opExtrude","SWEPT_FACE",FACE,{"disambiguationData":[OSD([subQ1,subQ0])]}),makeQuery(id+"F5.opExtrude","SWEPT_FACE",FACE,{"disambiguationData":[OSD([sQuery(id+"F4.wireOp",EDGE,"E7")])]}),makeQuery(id+"F5.opExtrude","SWEPT_FACE",FACE,{"disambiguationData":[OSD([sQuery(id+"F4.wireOp",EDGE,"E8")])]}),makeQuery(id+"F5.opExtrude","SWEPT_FACE",FACE,{"disambiguationData":[OSD([sQuery(id+"F4.wireOp",EDGE,"E9")])]}),makeQuery(id+"F7.opExtrude","SWEPT_FACE",FACE,{"disambiguationData":[OSD([subQ2])]}),makeQuery(id+"F7.opExtrude","CAP_FACE",FACE,{"disambiguationData":[OSD([subQ2,sQuery(id+"F6.wireOp",EDGE,"E17")])],"isStart":true}),makeQuery(id+"F7.opExtrude","CAP_FACE",FACE,{"disambiguationData":[OSD([subQ1,subQ0,sQuery(id+"F6.wireOp",EDGE,"E18.1.0.0")])],"isStart":true}),makeQuery(id+"F7.opExtrude","CAP_FACE",FACE,{"disambiguationData":[OSD([subQ1,subQ0,sQuery(id+"F6.wireOp",EDGE,"E18.2.0.0")])],"isStart":true}),makeQuery(id+"F7.opExtrude","CAP_FACE",FACE,{"disambiguationData":[OSD([subQ1,subQ0,sQuery(id+"F6.wireOp",EDGE,"E18.3.0.0")])],"isStart":true}),makeQuery(id+"F7.opExtrude","CAP_FACE",FACE,{"disambiguationData":[OSD([subQ1,subQ0,sQuery(id+"F6.wireOp",EDGE,"E18.4.0.0")])],"isStart":true}),makeQuery(id+"F7.opExtrude","CAP_FACE",FACE,{"disambiguationData":[OSD([subQ1,subQ0,sQuery(id+"F6.wireOp",EDGE,"E18.5.0.0")])],"isStart":true}),makeQuery(id+"F7.opExtrude","CAP_FACE",FACE,{"disambiguationData":[OSD([subQ1,subQ0,sQuery(id+"F6.wireOp",EDGE,"E18.6.0.0")])],"isStart":true}),makeQuery(id+"F7.opExtrude","CAP_FACE",FACE,{"disambiguationData":[OSD([subQ1,subQ0,sQuery(id+"F6.wireOp",EDGE,"E18.7.0.0")])],"isStart":true}),makeQuery(id+"F7.opExtrude","CAP_FACE",FACE,{"disambiguationData":[OSD([subQ1,subQ0,sQuery(id+"F6.wireOp",EDGE,"E18.8.0.0")])],"isStart":true}),makeQuery(id+"F7.opExtrude","CAP_FACE",FACE,{"disambiguationData":[OSD([subQ1,subQ0,sQuery(id+"F6.wireOp",EDGE,"E18.9.0.0")])],"isStart":true})])],"derivedFrom":makeQuery(id+"F3.opExtrude","CAP_FACE",FACE,{"disambiguationData":[OSD([sQuery(id+"F2.wireOp",EDGE,"E0"),subQ3,subQ1,sQuery(id+"F2.wireOp",EDGE,"E3.MirrorCS"),sQuery(id+"F2.wireOp",EDGE,"E4.MirrorCS"),subQ0])],"isStart":false})});}
            var sketch = newSketch(context, id + "F28", { "sketchPlane" : qUnion([Q0])});
            skCircle(sketch, "E69", {"center": v(23.57, 45) * mm, "radius": 5 * mm});
            skCircle(sketch, "E70", {"center": v(-23.57, 45) * mm, "radius": 5 * mm});
            skCircle(sketch, "E71", {"center": v(-23.57, 15) * mm, "radius": 5 * mm});
            skCircle(sketch, "E72", {"center": v(23.57, 15) * mm, "radius": 5 * mm});
            skCircle(sketch, "E73", {"center": v(0, 10) * mm, "radius": 5 * mm});
            skSolve(sketch);
        }
        {
            var Q0;
            Q0 = qSketchRegion(id + "F28", true);
            extrude(context, id + "F29", {"entities" : qUnion([Q0]), "operationType" : NewBodyOperationType.REMOVE, "depth" : 25 * mm});
        }
        {
            var Q0;
            Q0=makeQuery(id+"F3.opExtrude","CAP_FACE",FACE,{"disambiguationData":[OSD([sQuery(id+"F2.wireOp",EDGE,"E0"),sQuery(id+"F2.wireOp",EDGE,"E1"),sQuery(id+"F2.wireOp",EDGE,"E2"),sQuery(id+"F2.wireOp",EDGE,"E3.MirrorCS"),sQuery(id+"F2.wireOp",EDGE,"E4.MirrorCS"),sQuery(id+"F2.wireOp",EDGE,"E5.MirrorCS")])],"isStart":true});
            var sketch = newSketch(context, id + "F30", { "sketchPlane" : qUnion([Q0])});
            skArc(sketch, "E74", {"start": v(60, 0) * mm, "mid": v(55.9, 57.85) * mm, "end": v(27.05, 108.16) * mm});
            skPoint(sketch, "E75", {"position": v(-23.57, 15) * mm});
            skLineSegment(sketch, "E76", {"start": v(-31.57, 0) * mm, "end": v(-31.57, 90) * mm});
            skLineSegment(sketch, "E77", {"start": v(0, 90) * mm, "end": v(-31.57, 90) * mm});
            skArc(sketch, "E78.MirrorCS", {"start": v(-60, 0) * mm, "mid": v(-55.9, 57.85) * mm, "end": v(-27.05, 108.16) * mm});
            skPoint(sketch, "E79.MirrorP", {"position": v(23.57, 15) * mm});
            skLineSegment(sketch, "E80.MirrorCS", {"start": v(31.57, 0) * mm, "end": v(31.57, 90) * mm});
            skLineSegment(sketch, "E81.MirrorCS", {"start": v(0, 90) * mm, "end": v(31.57, 90) * mm});
            skLineSegment(sketch, "E82", {"start": v(-15.57, 0) * mm, "end": v(-15.57, 60) * mm});
            skLineSegment(sketch, "E83", {"start": v(-15.57, 60) * mm, "end": v(-31.57, 60) * mm});
            skPoint(sketch, "E84", {"position": v(-23.57, 45) * mm});
            skLineSegment(sketch, "E85.MirrorCS", {"start": v(15.57, 60) * mm, "end": v(31.57, 60) * mm});
            skLineSegment(sketch, "E86.MirrorCS", {"start": v(15.57, 0) * mm, "end": v(15.57, 60) * mm});
            skLineSegment(sketch, "E87", {"start": v(-27.05, 108.16) * mm, "end": v(27.05, 108.16) * mm});
            skLineSegment(sketch, "E88", {"start": v(-60, 0) * mm, "end": v(-31.57, 0) * mm});
            skLineSegment(sketch, "E89", {"start": v(31.57, 0) * mm, "end": v(60, 0) * mm});
            skLineSegment(sketch, "E90", {"start": v(-15.57, 0) * mm, "end": v(-7.5, 0) * mm});
            skLineSegment(sketch, "E91", {"start": v(-7.5, 0) * mm, "end": v(-7.5, 20) * mm});
            skLineSegment(sketch, "E92", {"start": v(-7.5, 20) * mm, "end": v(7.5, 20) * mm});
            skLineSegment(sketch, "E93", {"start": v(7.5, 20) * mm, "end": v(7.5, 0) * mm});
            skLineSegment(sketch, "E94", {"start": v(7.5, 0) * mm, "end": v(15.57, 0) * mm});
            skPoint(sketch, "E95", {"position": v(0, 20) * mm});
            skPoint(sketch, "E96", {"position": v(0, 0) * mm});
            skSolve(sketch);
        }
        {
            var Q0;
            Q0 = qSketchRegion(id + "F30", true);
            extrude(context, id + "F31", {"entities" : qUnion([Q0]), "operationType" : NewBodyOperationType.ADD, "depth" : 3 * mm});
        }
        {
            var Q0;
            Q0=makeQuery(id+"F31.opExtrude","SWEPT_EDGE",EDGE,{"disambiguationData":[OSD([sQuery(id+"F30.wireOp",EDGE,"E76"),sQuery(id+"F30.wireOp",EDGE,"E77")])]});
            var Q1;
            Q1=makeQuery(id+"F31.opExtrude","SWEPT_EDGE",EDGE,{"disambiguationData":[OSD([sQuery(id+"F30.wireOp",EDGE,"E80.MirrorCS"),sQuery(id+"F30.wireOp",EDGE,"E81.MirrorCS")])]});
            fillet(context, id + "F32", {"entities" : qUnion([Q0, Q1]), "radius" : 5 * mm, "tangentPropagation" : true, "allowEdgeOverflow" : false});
        }
        {
            var Q0;
            Q0=makeQuery(id+"F31.opExtrude","CAP_EDGE",EDGE,{"disambiguationData":[OSD([sQuery(id+"F30.wireOp",EDGE,"E74")])],"isStart":false});
            var Q1;
            Q1=makeQuery(id+"F5.opExtrude","CAP_EDGE",EDGE,{"disambiguationData":[OSD([sQuery(id+"F4.wireOp",EDGE,"E7")])],"isStart":false});
            var Q2;
            Q2=makeQuery(id+"F5.opExtrude","CAP_EDGE",EDGE,{"disambiguationData":[OSD([sQuery(id+"F4.wireOp",EDGE,"E8")])],"isStart":false});
            var Q3;
            Q3=makeQuery(id+"F5.opExtrude","CAP_EDGE",EDGE,{"disambiguationData":[OSD([sQuery(id+"F4.wireOp",EDGE,"E14")])],"isStart":false});
            var Q4;
            Q4=makeQuery(id+"F5.opExtrude","CAP_EDGE",EDGE,{"disambiguationData":[OSD([sQuery(id+"F4.wireOp",EDGE,"E10.MirrorCS")])],"isStart":false});
            var Q5;
            Q5=makeQuery(id+"F31.opExtrude","CAP_EDGE",EDGE,{"disambiguationData":[OSD([sQuery(id+"F30.wireOp",EDGE,"E87")])],"isStart":false});
            var Q6;
            Q6=makeQuery(id+"F31.opExtrude","CAP_EDGE",EDGE,{"disambiguationData":[OSD([sQuery(id+"F30.wireOp",EDGE,"E78.MirrorCS")])],"isStart":false});
            var Q7;
            Q7=makeQuery(id+"F31.opExtrude","CAP_EDGE",EDGE,{"disambiguationData":[OSD([sQuery(id+"F30.wireOp",EDGE,"E89")])],"isStart":false});
            var Q8;
            Q8=makeQuery(id+"F31.opExtrude","CAP_EDGE",EDGE,{"disambiguationData":[OSD([sQuery(id+"F30.wireOp",EDGE,"SiEx8vhQ-fxaC-5RrE-m7GO-d7uEWHyiGlIe")])],"isStart":false});
            var Q9;
            Q9=makeQuery(id+"F31.opExtrude","CAP_EDGE",EDGE,{"disambiguationData":[OSD([sQuery(id+"F30.wireOp",EDGE,"E88")])],"isStart":false});
            var Q10;
            Q10=makeQuery(id+"F31.boolean.opBoolean","MERGE",EDGE,{"derivedFrom":[makeQuery(id+"F5.boolean.opBoolean","MERGE",EDGE,{"derivedFrom":[makeQuery(id+"F3.opExtrude","SWEPT_EDGE",EDGE,{"disambiguationData":[OSD([sQuery(id+"F2.wireOp",EDGE,"E4.MirrorCS"),sQuery(id+"F2.wireOp",EDGE,"E5.MirrorCS")])]}),makeQuery(id+"F5.opExtrude","SWEPT_EDGE",EDGE,{"disambiguationData":[OSD([sQuery(id+"F4.wireOp",EDGE,"E11.MirrorCS"),sQuery(id+"F4.wireOp",EDGE,"E12.MirrorCS")])]})]}),makeQuery(id+"F31.opExtrude","SWEPT_EDGE",EDGE,{"disambiguationData":[OSD([sQuery(id+"F30.wireOp",EDGE,"E78.MirrorCS"),sQuery(id+"F30.wireOp",EDGE,"E88")])]})]});
            var Q11;
            Q11=makeQuery(id+"F31.boolean.opBoolean","MERGE",EDGE,{"derivedFrom":[makeQuery(id+"F5.boolean.opBoolean","MERGE",EDGE,{"derivedFrom":[makeQuery(id+"F3.opExtrude","SWEPT_EDGE",EDGE,{"disambiguationData":[OSD([sQuery(id+"F2.wireOp",EDGE,"E1"),sQuery(id+"F2.wireOp",EDGE,"E2")])]}),makeQuery(id+"F5.opExtrude","SWEPT_EDGE",EDGE,{"disambiguationData":[OSD([sQuery(id+"F4.wireOp",EDGE,"E7"),sQuery(id+"F4.wireOp",EDGE,"E9")])]})]}),makeQuery(id+"F31.opExtrude","SWEPT_EDGE",EDGE,{"disambiguationData":[OSD([sQuery(id+"F30.wireOp",EDGE,"E74"),sQuery(id+"F30.wireOp",EDGE,"E89")])]})]});
            chamfer(context, id + "F33", {"entities" : qUnion([Q0, Q1, Q2, Q3, Q4, Q5, Q6, Q7, Q8, Q9, Q10, Q11]), "width" : 2 * mm, "tangentPropagation" : true});
        }
        {
            var Q0;
            Q0=makeQuery(id+"F31.opExtrude","CAP_EDGE",EDGE,{"disambiguationData":[OSD([sQuery(id+"F30.wireOp",EDGE,"E80.MirrorCS")])],"isStart":false});
            var Q1;
            Q1=makeQuery(id+"F31.opExtrude","CAP_EDGE",EDGE,{"disambiguationData":[OSD([sQuery(id+"F30.wireOp",EDGE,"E85.MirrorCS")])],"isStart":false});
            var Q2;
            Q2=makeQuery(id+"F31.opExtrude","CAP_EDGE",EDGE,{"disambiguationData":[OSD([sQuery(id+"F30.wireOp",EDGE,"E86.MirrorCS")])],"isStart":false});
            var Q3;
            Q3=makeQuery(id+"F31.opExtrude","CAP_EDGE",EDGE,{"disambiguationData":[OSD([sQuery(id+"F30.wireOp",EDGE,"E76")])],"isStart":false});
            var Q4;
            Q4=makeQuery(id+"F31.opExtrude","CAP_EDGE",EDGE,{"disambiguationData":[OSD([sQuery(id+"F30.wireOp",EDGE,"E83")])],"isStart":false});
            var Q5;
            Q5=makeQuery(id+"F31.opExtrude","CAP_EDGE",EDGE,{"disambiguationData":[OSD([sQuery(id+"F30.wireOp",EDGE,"E82")])],"isStart":false});
            var Q6;
            Q6=makeQuery(id+"F31.opExtrude","CAP_EDGE",EDGE,{"disambiguationData":[OSD([sQuery(id+"F30.wireOp",EDGE,"E78.MirrorCS")])],"isStart":false});
            var Q7;
            Q7=makeQuery(id+"F31.opExtrude","CAP_EDGE",EDGE,{"disambiguationData":[OSD([sQuery(id+"F30.wireOp",EDGE,"E74")])],"isStart":false});
            var Q8;
            Q8=makeQuery(id+"F31.opExtrude","CAP_EDGE",EDGE,{"disambiguationData":[OSD([sQuery(id+"F30.wireOp",EDGE,"E91")])],"isStart":false});
            var Q9;
            Q9=makeQuery(id+"F31.opExtrude","CAP_EDGE",EDGE,{"disambiguationData":[OSD([sQuery(id+"F30.wireOp",EDGE,"E92")])],"isStart":false});
            var Q10;
            Q10=makeQuery(id+"F31.opExtrude","CAP_EDGE",EDGE,{"disambiguationData":[OSD([sQuery(id+"F30.wireOp",EDGE,"E93")])],"isStart":false});
            chamfer(context, id + "F34", {"entities" : qUnion([Q0, Q1, Q2, Q3, Q4, Q5, Q6, Q7, Q8, Q9, Q10]), "width" : 3 * mm, "tangentPropagation" : true});
        }
        {
            var Q0;
            {var subQ0=sQuery(id+"F2.wireOp",EDGE,"E5.MirrorCS");var subQ1=sQuery(id+"F2.wireOp",EDGE,"E2");var subQ2=sQuery(id+"F6.wireOp",EDGE,"E16");Q0=makeQuery(id+"F7.boolean.opBoolean","SPLIT",EDGE,{"disambiguationData":[TD([makeQuery(id+"F3.opExtrude","CAP_FACE",FACE,{"disambiguationData":[OSD([sQuery(id+"F2.wireOp",EDGE,"E0"),sQuery(id+"F2.wireOp",EDGE,"E1"),subQ1,sQuery(id+"F2.wireOp",EDGE,"E3.MirrorCS"),sQuery(id+"F2.wireOp",EDGE,"E4.MirrorCS"),subQ0])],"isStart":false}),makeQuery(id+"F3.opExtrude","SWEPT_FACE",FACE,{"disambiguationData":[OSD([subQ1,subQ0])]}),makeQuery(id+"F5.opExtrude","SWEPT_FACE",FACE,{"disambiguationData":[OSD([sQuery(id+"F4.wireOp",EDGE,"E8")])]}),makeQuery(id+"F5.opExtrude","SWEPT_FACE",FACE,{"disambiguationData":[OSD([sQuery(id+"F4.wireOp",EDGE,"E9")])]}),makeQuery(id+"F5.opExtrude","SWEPT_FACE",FACE,{"disambiguationData":[OSD([sQuery(id+"F4.wireOp",EDGE,"E11.MirrorCS")])]}),makeQuery(id+"F7.opExtrude","SWEPT_FACE",FACE,{"disambiguationData":[OSD([subQ2])]}),makeQuery(id+"F7.opExtrude","CAP_FACE",FACE,{"disambiguationData":[OSD([subQ2,sQuery(id+"F6.wireOp",EDGE,"E17")])],"isStart":true}),makeQuery(id+"F7.opExtrude","CAP_FACE",FACE,{"disambiguationData":[OSD([subQ1,subQ0,sQuery(id+"F6.wireOp",EDGE,"E18.1.0.0")])],"isStart":true}),makeQuery(id+"F7.opExtrude","CAP_FACE",FACE,{"disambiguationData":[OSD([subQ1,subQ0,sQuery(id+"F6.wireOp",EDGE,"E18.2.0.0")])],"isStart":true}),makeQuery(id+"F7.opExtrude","CAP_FACE",FACE,{"disambiguationData":[OSD([subQ1,subQ0,sQuery(id+"F6.wireOp",EDGE,"E18.3.0.0")])],"isStart":true}),makeQuery(id+"F7.opExtrude","CAP_FACE",FACE,{"disambiguationData":[OSD([subQ1,subQ0,sQuery(id+"F6.wireOp",EDGE,"E18.4.0.0")])],"isStart":true}),makeQuery(id+"F7.opExtrude","CAP_FACE",FACE,{"disambiguationData":[OSD([subQ1,subQ0,sQuery(id+"F6.wireOp",EDGE,"E18.5.0.0")])],"isStart":true}),makeQuery(id+"F7.opExtrude","CAP_FACE",FACE,{"disambiguationData":[OSD([subQ1,subQ0,sQuery(id+"F6.wireOp",EDGE,"E18.6.0.0")])],"isStart":true}),makeQuery(id+"F7.opExtrude","CAP_FACE",FACE,{"disambiguationData":[OSD([subQ1,subQ0,sQuery(id+"F6.wireOp",EDGE,"E18.7.0.0")])],"isStart":true}),makeQuery(id+"F7.opExtrude","CAP_FACE",FACE,{"disambiguationData":[OSD([subQ1,subQ0,sQuery(id+"F6.wireOp",EDGE,"E18.8.0.0")])],"isStart":true}),makeQuery(id+"F7.opExtrude","CAP_FACE",FACE,{"disambiguationData":[OSD([subQ1,subQ0,sQuery(id+"F6.wireOp",EDGE,"E18.9.0.0")])],"isStart":true})])],"derivedFrom":makeQuery(id+"F3.opExtrude","CAP_EDGE",EDGE,{"disambiguationData":[OSD([subQ1,subQ0])],"isStart":false})});}
            chamfer(context, id + "F35", {"entities" : qUnion([Q0]), "width" : 1 * mm, "tangentPropagation" : true});
        }
        {
            var Q0;
            Q0=makeQuery(id+"F31.opExtrude","CAP_EDGE",EDGE,{"disambiguationData":[OSD([sQuery(id+"F30.wireOp",EDGE,"LmbyR1he-35kO-f53Q-696j-YAIKVnODTwI9")])],"isStart":false});
            var Q1;
            {var subQ0=sQuery(id+"F2.wireOp",EDGE,"E5.MirrorCS");var subQ1=sQuery(id+"F2.wireOp",EDGE,"E2");Q1=makeQuery(id+"F34.opChamfer","BLEND_EDGE",EDGE,{"blendedFrom":[makeQuery(id+"F31.opExtrude","CAP_EDGE",EDGE,{"disambiguationData":[OSD([sQuery(id+"F30.wireOp",EDGE,"E82")])],"isStart":false}),makeQuery(id+"F31.boolean.opBoolean","MERGE",FACE,{"derivedFrom":[makeQuery(id+"F7.boolean.opBoolean","MERGE",FACE,{"derivedFrom":[makeQuery(id+"F5.boolean.opBoolean","MERGE",FACE,{"derivedFrom":[makeQuery(id+"F3.opExtrude","SWEPT_FACE",FACE,{"disambiguationData":[OSD([subQ1,subQ0])]}),makeQuery(id+"F5.opExtrude","SWEPT_FACE",FACE,{"disambiguationData":[OSD([sQuery(id+"F4.wireOp",EDGE,"E9")])]}),makeQuery(id+"F5.opExtrude","SWEPT_FACE",FACE,{"disambiguationData":[OSD([sQuery(id+"F4.wireOp",EDGE,"E11.MirrorCS")])]})]}),makeQuery(id+"F7.opExtrude","CAP_FACE",FACE,{"disambiguationData":[OSD([sQuery(id+"F6.wireOp",EDGE,"E16"),sQuery(id+"F6.wireOp",EDGE,"E17")])],"isStart":true}),makeQuery(id+"F7.opExtrude","CAP_FACE",FACE,{"disambiguationData":[OSD([subQ1,subQ0,sQuery(id+"F6.wireOp",EDGE,"E18.1.0.0")])],"isStart":true}),makeQuery(id+"F7.opExtrude","CAP_FACE",FACE,{"disambiguationData":[OSD([subQ1,subQ0,sQuery(id+"F6.wireOp",EDGE,"E18.2.0.0")])],"isStart":true}),makeQuery(id+"F7.opExtrude","CAP_FACE",FACE,{"disambiguationData":[OSD([subQ1,subQ0,sQuery(id+"F6.wireOp",EDGE,"E18.3.0.0")])],"isStart":true}),makeQuery(id+"F7.opExtrude","CAP_FACE",FACE,{"disambiguationData":[OSD([subQ1,subQ0,sQuery(id+"F6.wireOp",EDGE,"E18.4.0.0")])],"isStart":true}),makeQuery(id+"F7.opExtrude","CAP_FACE",FACE,{"disambiguationData":[OSD([subQ1,subQ0,sQuery(id+"F6.wireOp",EDGE,"E18.5.0.0")])],"isStart":true}),makeQuery(id+"F7.opExtrude","CAP_FACE",FACE,{"disambiguationData":[OSD([subQ1,subQ0,sQuery(id+"F6.wireOp",EDGE,"E18.6.0.0")])],"isStart":true}),makeQuery(id+"F7.opExtrude","CAP_FACE",FACE,{"disambiguationData":[OSD([subQ1,subQ0,sQuery(id+"F6.wireOp",EDGE,"E18.7.0.0")])],"isStart":true}),makeQuery(id+"F7.opExtrude","CAP_FACE",FACE,{"disambiguationData":[OSD([subQ1,subQ0,sQuery(id+"F6.wireOp",EDGE,"E18.8.0.0")])],"isStart":true}),makeQuery(id+"F7.opExtrude","CAP_FACE",FACE,{"disambiguationData":[OSD([subQ1,subQ0,sQuery(id+"F6.wireOp",EDGE,"E18.9.0.0")])],"isStart":true})]}),makeQuery(id+"F31.opExtrude","SWEPT_FACE",FACE,{"disambiguationData":[OSD([sQuery(id+"F30.wireOp",EDGE,"LmbyR1he-35kO-f53Q-696j-YAIKVnODTwI9")])]}),makeQuery(id+"F31.opExtrude","SWEPT_FACE",FACE,{"disambiguationData":[OSD([sQuery(id+"F30.wireOp",EDGE,"lc0urJVt-xGFD-1UqV-AUzd-Ddt8hkDyLtwQ"),sQuery(id+"F30.wireOp",EDGE,"9e28845e-500e-4894-8802-eb7ad12137a13.MirrorCS")])]}),makeQuery(id+"F31.opExtrude","SWEPT_FACE",FACE,{"disambiguationData":[OSD([sQuery(id+"F30.wireOp",EDGE,"9e28845e-500e-4894-8802-eb7ad12137a10.MirrorCS")])]})]})],"blendedInto":[makeQuery(id+"F31.boolean.opBoolean","MERGE",FACE,{"derivedFrom":[makeQuery(id+"F7.boolean.opBoolean","MERGE",FACE,{"derivedFrom":[makeQuery(id+"F5.boolean.opBoolean","MERGE",FACE,{"derivedFrom":[makeQuery(id+"F3.opExtrude","SWEPT_FACE",FACE,{"disambiguationData":[OSD([subQ1,subQ0])]}),makeQuery(id+"F5.opExtrude","SWEPT_FACE",FACE,{"disambiguationData":[OSD([sQuery(id+"F4.wireOp",EDGE,"E9")])]}),makeQuery(id+"F5.opExtrude","SWEPT_FACE",FACE,{"disambiguationData":[OSD([sQuery(id+"F4.wireOp",EDGE,"E11.MirrorCS")])]})]}),makeQuery(id+"F7.opExtrude","CAP_FACE",FACE,{"disambiguationData":[OSD([sQuery(id+"F6.wireOp",EDGE,"E16"),sQuery(id+"F6.wireOp",EDGE,"E17")])],"isStart":true}),makeQuery(id+"F7.opExtrude","CAP_FACE",FACE,{"disambiguationData":[OSD([subQ1,subQ0,sQuery(id+"F6.wireOp",EDGE,"E18.1.0.0")])],"isStart":true}),makeQuery(id+"F7.opExtrude","CAP_FACE",FACE,{"disambiguationData":[OSD([subQ1,subQ0,sQuery(id+"F6.wireOp",EDGE,"E18.2.0.0")])],"isStart":true}),makeQuery(id+"F7.opExtrude","CAP_FACE",FACE,{"disambiguationData":[OSD([subQ1,subQ0,sQuery(id+"F6.wireOp",EDGE,"E18.3.0.0")])],"isStart":true}),makeQuery(id+"F7.opExtrude","CAP_FACE",FACE,{"disambiguationData":[OSD([subQ1,subQ0,sQuery(id+"F6.wireOp",EDGE,"E18.4.0.0")])],"isStart":true}),makeQuery(id+"F7.opExtrude","CAP_FACE",FACE,{"disambiguationData":[OSD([subQ1,subQ0,sQuery(id+"F6.wireOp",EDGE,"E18.5.0.0")])],"isStart":true}),makeQuery(id+"F7.opExtrude","CAP_FACE",FACE,{"disambiguationData":[OSD([subQ1,subQ0,sQuery(id+"F6.wireOp",EDGE,"E18.6.0.0")])],"isStart":true}),makeQuery(id+"F7.opExtrude","CAP_FACE",FACE,{"disambiguationData":[OSD([subQ1,subQ0,sQuery(id+"F6.wireOp",EDGE,"E18.7.0.0")])],"isStart":true}),makeQuery(id+"F7.opExtrude","CAP_FACE",FACE,{"disambiguationData":[OSD([subQ1,subQ0,sQuery(id+"F6.wireOp",EDGE,"E18.8.0.0")])],"isStart":true}),makeQuery(id+"F7.opExtrude","CAP_FACE",FACE,{"disambiguationData":[OSD([subQ1,subQ0,sQuery(id+"F6.wireOp",EDGE,"E18.9.0.0")])],"isStart":true})]}),makeQuery(id+"F31.opExtrude","SWEPT_FACE",FACE,{"disambiguationData":[OSD([sQuery(id+"F30.wireOp",EDGE,"LmbyR1he-35kO-f53Q-696j-YAIKVnODTwI9")])]}),makeQuery(id+"F31.opExtrude","SWEPT_FACE",FACE,{"disambiguationData":[OSD([sQuery(id+"F30.wireOp",EDGE,"lc0urJVt-xGFD-1UqV-AUzd-Ddt8hkDyLtwQ"),sQuery(id+"F30.wireOp",EDGE,"9e28845e-500e-4894-8802-eb7ad12137a13.MirrorCS")])]}),makeQuery(id+"F31.opExtrude","SWEPT_FACE",FACE,{"disambiguationData":[OSD([sQuery(id+"F30.wireOp",EDGE,"9e28845e-500e-4894-8802-eb7ad12137a10.MirrorCS")])]})]})]});}
            var Q2;
            {var subQ0=sQuery(id+"F2.wireOp",EDGE,"E5.MirrorCS");var subQ1=sQuery(id+"F2.wireOp",EDGE,"E2");Q2=makeQuery(id+"F31.boolean.opBoolean","SPLIT",EDGE,{"disambiguationData":[TD([makeQuery(id+"F31.opExtrude","SWEPT_FACE",FACE,{"disambiguationData":[OSD([sQuery(id+"F30.wireOp",EDGE,"E76")])]})])],"derivedFrom":makeQuery(id+"F3.opExtrude","CAP_EDGE",EDGE,{"disambiguationData":[OSD([subQ1,subQ0])],"isStart":true})});}
            var Q3;
            {var subQ0=sQuery(id+"F2.wireOp",EDGE,"E5.MirrorCS");var subQ1=sQuery(id+"F2.wireOp",EDGE,"E2");Q3=makeQuery(id+"F34.opChamfer","BLEND_EDGE",EDGE,{"blendedFrom":[makeQuery(id+"F31.opExtrude","CAP_EDGE",EDGE,{"disambiguationData":[OSD([sQuery(id+"F30.wireOp",EDGE,"E76")])],"isStart":false}),makeQuery(id+"F31.boolean.opBoolean","MERGE",FACE,{"derivedFrom":[makeQuery(id+"F7.boolean.opBoolean","MERGE",FACE,{"derivedFrom":[makeQuery(id+"F5.boolean.opBoolean","MERGE",FACE,{"derivedFrom":[makeQuery(id+"F3.opExtrude","SWEPT_FACE",FACE,{"disambiguationData":[OSD([subQ1,subQ0])]}),makeQuery(id+"F5.opExtrude","SWEPT_FACE",FACE,{"disambiguationData":[OSD([sQuery(id+"F4.wireOp",EDGE,"E9")])]}),makeQuery(id+"F5.opExtrude","SWEPT_FACE",FACE,{"disambiguationData":[OSD([sQuery(id+"F4.wireOp",EDGE,"E11.MirrorCS")])]})]}),makeQuery(id+"F7.opExtrude","CAP_FACE",FACE,{"disambiguationData":[OSD([sQuery(id+"F6.wireOp",EDGE,"E16"),sQuery(id+"F6.wireOp",EDGE,"E17")])],"isStart":true}),makeQuery(id+"F7.opExtrude","CAP_FACE",FACE,{"disambiguationData":[OSD([subQ1,subQ0,sQuery(id+"F6.wireOp",EDGE,"E18.1.0.0")])],"isStart":true}),makeQuery(id+"F7.opExtrude","CAP_FACE",FACE,{"disambiguationData":[OSD([subQ1,subQ0,sQuery(id+"F6.wireOp",EDGE,"E18.2.0.0")])],"isStart":true}),makeQuery(id+"F7.opExtrude","CAP_FACE",FACE,{"disambiguationData":[OSD([subQ1,subQ0,sQuery(id+"F6.wireOp",EDGE,"E18.3.0.0")])],"isStart":true}),makeQuery(id+"F7.opExtrude","CAP_FACE",FACE,{"disambiguationData":[OSD([subQ1,subQ0,sQuery(id+"F6.wireOp",EDGE,"E18.4.0.0")])],"isStart":true}),makeQuery(id+"F7.opExtrude","CAP_FACE",FACE,{"disambiguationData":[OSD([subQ1,subQ0,sQuery(id+"F6.wireOp",EDGE,"E18.5.0.0")])],"isStart":true}),makeQuery(id+"F7.opExtrude","CAP_FACE",FACE,{"disambiguationData":[OSD([subQ1,subQ0,sQuery(id+"F6.wireOp",EDGE,"E18.6.0.0")])],"isStart":true}),makeQuery(id+"F7.opExtrude","CAP_FACE",FACE,{"disambiguationData":[OSD([subQ1,subQ0,sQuery(id+"F6.wireOp",EDGE,"E18.7.0.0")])],"isStart":true}),makeQuery(id+"F7.opExtrude","CAP_FACE",FACE,{"disambiguationData":[OSD([subQ1,subQ0,sQuery(id+"F6.wireOp",EDGE,"E18.8.0.0")])],"isStart":true}),makeQuery(id+"F7.opExtrude","CAP_FACE",FACE,{"disambiguationData":[OSD([subQ1,subQ0,sQuery(id+"F6.wireOp",EDGE,"E18.9.0.0")])],"isStart":true})]}),makeQuery(id+"F31.opExtrude","SWEPT_FACE",FACE,{"disambiguationData":[OSD([sQuery(id+"F30.wireOp",EDGE,"LmbyR1he-35kO-f53Q-696j-YAIKVnODTwI9")])]}),makeQuery(id+"F31.opExtrude","SWEPT_FACE",FACE,{"disambiguationData":[OSD([sQuery(id+"F30.wireOp",EDGE,"lc0urJVt-xGFD-1UqV-AUzd-Ddt8hkDyLtwQ"),sQuery(id+"F30.wireOp",EDGE,"9e28845e-500e-4894-8802-eb7ad12137a13.MirrorCS")])]}),makeQuery(id+"F31.opExtrude","SWEPT_FACE",FACE,{"disambiguationData":[OSD([sQuery(id+"F30.wireOp",EDGE,"9e28845e-500e-4894-8802-eb7ad12137a10.MirrorCS")])]})]})],"blendedInto":[makeQuery(id+"F31.boolean.opBoolean","MERGE",FACE,{"derivedFrom":[makeQuery(id+"F7.boolean.opBoolean","MERGE",FACE,{"derivedFrom":[makeQuery(id+"F5.boolean.opBoolean","MERGE",FACE,{"derivedFrom":[makeQuery(id+"F3.opExtrude","SWEPT_FACE",FACE,{"disambiguationData":[OSD([subQ1,subQ0])]}),makeQuery(id+"F5.opExtrude","SWEPT_FACE",FACE,{"disambiguationData":[OSD([sQuery(id+"F4.wireOp",EDGE,"E9")])]}),makeQuery(id+"F5.opExtrude","SWEPT_FACE",FACE,{"disambiguationData":[OSD([sQuery(id+"F4.wireOp",EDGE,"E11.MirrorCS")])]})]}),makeQuery(id+"F7.opExtrude","CAP_FACE",FACE,{"disambiguationData":[OSD([sQuery(id+"F6.wireOp",EDGE,"E16"),sQuery(id+"F6.wireOp",EDGE,"E17")])],"isStart":true}),makeQuery(id+"F7.opExtrude","CAP_FACE",FACE,{"disambiguationData":[OSD([subQ1,subQ0,sQuery(id+"F6.wireOp",EDGE,"E18.1.0.0")])],"isStart":true}),makeQuery(id+"F7.opExtrude","CAP_FACE",FACE,{"disambiguationData":[OSD([subQ1,subQ0,sQuery(id+"F6.wireOp",EDGE,"E18.2.0.0")])],"isStart":true}),makeQuery(id+"F7.opExtrude","CAP_FACE",FACE,{"disambiguationData":[OSD([subQ1,subQ0,sQuery(id+"F6.wireOp",EDGE,"E18.3.0.0")])],"isStart":true}),makeQuery(id+"F7.opExtrude","CAP_FACE",FACE,{"disambiguationData":[OSD([subQ1,subQ0,sQuery(id+"F6.wireOp",EDGE,"E18.4.0.0")])],"isStart":true}),makeQuery(id+"F7.opExtrude","CAP_FACE",FACE,{"disambiguationData":[OSD([subQ1,subQ0,sQuery(id+"F6.wireOp",EDGE,"E18.5.0.0")])],"isStart":true}),makeQuery(id+"F7.opExtrude","CAP_FACE",FACE,{"disambiguationData":[OSD([subQ1,subQ0,sQuery(id+"F6.wireOp",EDGE,"E18.6.0.0")])],"isStart":true}),makeQuery(id+"F7.opExtrude","CAP_FACE",FACE,{"disambiguationData":[OSD([subQ1,subQ0,sQuery(id+"F6.wireOp",EDGE,"E18.7.0.0")])],"isStart":true}),makeQuery(id+"F7.opExtrude","CAP_FACE",FACE,{"disambiguationData":[OSD([subQ1,subQ0,sQuery(id+"F6.wireOp",EDGE,"E18.8.0.0")])],"isStart":true}),makeQuery(id+"F7.opExtrude","CAP_FACE",FACE,{"disambiguationData":[OSD([subQ1,subQ0,sQuery(id+"F6.wireOp",EDGE,"E18.9.0.0")])],"isStart":true})]}),makeQuery(id+"F31.opExtrude","SWEPT_FACE",FACE,{"disambiguationData":[OSD([sQuery(id+"F30.wireOp",EDGE,"LmbyR1he-35kO-f53Q-696j-YAIKVnODTwI9")])]}),makeQuery(id+"F31.opExtrude","SWEPT_FACE",FACE,{"disambiguationData":[OSD([sQuery(id+"F30.wireOp",EDGE,"lc0urJVt-xGFD-1UqV-AUzd-Ddt8hkDyLtwQ"),sQuery(id+"F30.wireOp",EDGE,"9e28845e-500e-4894-8802-eb7ad12137a13.MirrorCS")])]}),makeQuery(id+"F31.opExtrude","SWEPT_FACE",FACE,{"disambiguationData":[OSD([sQuery(id+"F30.wireOp",EDGE,"9e28845e-500e-4894-8802-eb7ad12137a10.MirrorCS")])]})]})]});}
            var Q4;
            Q4=makeQuery(id+"F31.opExtrude","CAP_EDGE",EDGE,{"disambiguationData":[OSD([sQuery(id+"F30.wireOp",EDGE,"lc0urJVt-xGFD-1UqV-AUzd-Ddt8hkDyLtwQ"),sQuery(id+"F30.wireOp",EDGE,"9e28845e-500e-4894-8802-eb7ad12137a13.MirrorCS")])],"isStart":false});
            var Q5;
            {var subQ0=sQuery(id+"F2.wireOp",EDGE,"E5.MirrorCS");var subQ1=sQuery(id+"F2.wireOp",EDGE,"E2");Q5=makeQuery(id+"F34.opChamfer","BLEND_EDGE",EDGE,{"blendedFrom":[makeQuery(id+"F31.opExtrude","CAP_EDGE",EDGE,{"disambiguationData":[OSD([sQuery(id+"F30.wireOp",EDGE,"E80.MirrorCS")])],"isStart":false}),makeQuery(id+"F31.boolean.opBoolean","MERGE",FACE,{"derivedFrom":[makeQuery(id+"F7.boolean.opBoolean","MERGE",FACE,{"derivedFrom":[makeQuery(id+"F5.boolean.opBoolean","MERGE",FACE,{"derivedFrom":[makeQuery(id+"F3.opExtrude","SWEPT_FACE",FACE,{"disambiguationData":[OSD([subQ1,subQ0])]}),makeQuery(id+"F5.opExtrude","SWEPT_FACE",FACE,{"disambiguationData":[OSD([sQuery(id+"F4.wireOp",EDGE,"E9")])]}),makeQuery(id+"F5.opExtrude","SWEPT_FACE",FACE,{"disambiguationData":[OSD([sQuery(id+"F4.wireOp",EDGE,"E11.MirrorCS")])]})]}),makeQuery(id+"F7.opExtrude","CAP_FACE",FACE,{"disambiguationData":[OSD([sQuery(id+"F6.wireOp",EDGE,"E16"),sQuery(id+"F6.wireOp",EDGE,"E17")])],"isStart":true}),makeQuery(id+"F7.opExtrude","CAP_FACE",FACE,{"disambiguationData":[OSD([subQ1,subQ0,sQuery(id+"F6.wireOp",EDGE,"E18.1.0.0")])],"isStart":true}),makeQuery(id+"F7.opExtrude","CAP_FACE",FACE,{"disambiguationData":[OSD([subQ1,subQ0,sQuery(id+"F6.wireOp",EDGE,"E18.2.0.0")])],"isStart":true}),makeQuery(id+"F7.opExtrude","CAP_FACE",FACE,{"disambiguationData":[OSD([subQ1,subQ0,sQuery(id+"F6.wireOp",EDGE,"E18.3.0.0")])],"isStart":true}),makeQuery(id+"F7.opExtrude","CAP_FACE",FACE,{"disambiguationData":[OSD([subQ1,subQ0,sQuery(id+"F6.wireOp",EDGE,"E18.4.0.0")])],"isStart":true}),makeQuery(id+"F7.opExtrude","CAP_FACE",FACE,{"disambiguationData":[OSD([subQ1,subQ0,sQuery(id+"F6.wireOp",EDGE,"E18.5.0.0")])],"isStart":true}),makeQuery(id+"F7.opExtrude","CAP_FACE",FACE,{"disambiguationData":[OSD([subQ1,subQ0,sQuery(id+"F6.wireOp",EDGE,"E18.6.0.0")])],"isStart":true}),makeQuery(id+"F7.opExtrude","CAP_FACE",FACE,{"disambiguationData":[OSD([subQ1,subQ0,sQuery(id+"F6.wireOp",EDGE,"E18.7.0.0")])],"isStart":true}),makeQuery(id+"F7.opExtrude","CAP_FACE",FACE,{"disambiguationData":[OSD([subQ1,subQ0,sQuery(id+"F6.wireOp",EDGE,"E18.8.0.0")])],"isStart":true}),makeQuery(id+"F7.opExtrude","CAP_FACE",FACE,{"disambiguationData":[OSD([subQ1,subQ0,sQuery(id+"F6.wireOp",EDGE,"E18.9.0.0")])],"isStart":true})]}),makeQuery(id+"F31.opExtrude","SWEPT_FACE",FACE,{"disambiguationData":[OSD([sQuery(id+"F30.wireOp",EDGE,"LmbyR1he-35kO-f53Q-696j-YAIKVnODTwI9")])]}),makeQuery(id+"F31.opExtrude","SWEPT_FACE",FACE,{"disambiguationData":[OSD([sQuery(id+"F30.wireOp",EDGE,"lc0urJVt-xGFD-1UqV-AUzd-Ddt8hkDyLtwQ"),sQuery(id+"F30.wireOp",EDGE,"9e28845e-500e-4894-8802-eb7ad12137a13.MirrorCS")])]}),makeQuery(id+"F31.opExtrude","SWEPT_FACE",FACE,{"disambiguationData":[OSD([sQuery(id+"F30.wireOp",EDGE,"9e28845e-500e-4894-8802-eb7ad12137a10.MirrorCS")])]})]})],"blendedInto":[makeQuery(id+"F31.boolean.opBoolean","MERGE",FACE,{"derivedFrom":[makeQuery(id+"F7.boolean.opBoolean","MERGE",FACE,{"derivedFrom":[makeQuery(id+"F5.boolean.opBoolean","MERGE",FACE,{"derivedFrom":[makeQuery(id+"F3.opExtrude","SWEPT_FACE",FACE,{"disambiguationData":[OSD([subQ1,subQ0])]}),makeQuery(id+"F5.opExtrude","SWEPT_FACE",FACE,{"disambiguationData":[OSD([sQuery(id+"F4.wireOp",EDGE,"E9")])]}),makeQuery(id+"F5.opExtrude","SWEPT_FACE",FACE,{"disambiguationData":[OSD([sQuery(id+"F4.wireOp",EDGE,"E11.MirrorCS")])]})]}),makeQuery(id+"F7.opExtrude","CAP_FACE",FACE,{"disambiguationData":[OSD([sQuery(id+"F6.wireOp",EDGE,"E16"),sQuery(id+"F6.wireOp",EDGE,"E17")])],"isStart":true}),makeQuery(id+"F7.opExtrude","CAP_FACE",FACE,{"disambiguationData":[OSD([subQ1,subQ0,sQuery(id+"F6.wireOp",EDGE,"E18.1.0.0")])],"isStart":true}),makeQuery(id+"F7.opExtrude","CAP_FACE",FACE,{"disambiguationData":[OSD([subQ1,subQ0,sQuery(id+"F6.wireOp",EDGE,"E18.2.0.0")])],"isStart":true}),makeQuery(id+"F7.opExtrude","CAP_FACE",FACE,{"disambiguationData":[OSD([subQ1,subQ0,sQuery(id+"F6.wireOp",EDGE,"E18.3.0.0")])],"isStart":true}),makeQuery(id+"F7.opExtrude","CAP_FACE",FACE,{"disambiguationData":[OSD([subQ1,subQ0,sQuery(id+"F6.wireOp",EDGE,"E18.4.0.0")])],"isStart":true}),makeQuery(id+"F7.opExtrude","CAP_FACE",FACE,{"disambiguationData":[OSD([subQ1,subQ0,sQuery(id+"F6.wireOp",EDGE,"E18.5.0.0")])],"isStart":true}),makeQuery(id+"F7.opExtrude","CAP_FACE",FACE,{"disambiguationData":[OSD([subQ1,subQ0,sQuery(id+"F6.wireOp",EDGE,"E18.6.0.0")])],"isStart":true}),makeQuery(id+"F7.opExtrude","CAP_FACE",FACE,{"disambiguationData":[OSD([subQ1,subQ0,sQuery(id+"F6.wireOp",EDGE,"E18.7.0.0")])],"isStart":true}),makeQuery(id+"F7.opExtrude","CAP_FACE",FACE,{"disambiguationData":[OSD([subQ1,subQ0,sQuery(id+"F6.wireOp",EDGE,"E18.8.0.0")])],"isStart":true}),makeQuery(id+"F7.opExtrude","CAP_FACE",FACE,{"disambiguationData":[OSD([subQ1,subQ0,sQuery(id+"F6.wireOp",EDGE,"E18.9.0.0")])],"isStart":true})]}),makeQuery(id+"F31.opExtrude","SWEPT_FACE",FACE,{"disambiguationData":[OSD([sQuery(id+"F30.wireOp",EDGE,"LmbyR1he-35kO-f53Q-696j-YAIKVnODTwI9")])]}),makeQuery(id+"F31.opExtrude","SWEPT_FACE",FACE,{"disambiguationData":[OSD([sQuery(id+"F30.wireOp",EDGE,"lc0urJVt-xGFD-1UqV-AUzd-Ddt8hkDyLtwQ"),sQuery(id+"F30.wireOp",EDGE,"9e28845e-500e-4894-8802-eb7ad12137a13.MirrorCS")])]}),makeQuery(id+"F31.opExtrude","SWEPT_FACE",FACE,{"disambiguationData":[OSD([sQuery(id+"F30.wireOp",EDGE,"9e28845e-500e-4894-8802-eb7ad12137a10.MirrorCS")])]})]})]});}
            var Q6;
            {var subQ0=sQuery(id+"F2.wireOp",EDGE,"E5.MirrorCS");var subQ1=sQuery(id+"F2.wireOp",EDGE,"E2");Q6=makeQuery(id+"F31.boolean.opBoolean","SPLIT",EDGE,{"disambiguationData":[TD([makeQuery(id+"F31.opExtrude","SWEPT_FACE",FACE,{"disambiguationData":[OSD([sQuery(id+"F30.wireOp",EDGE,"E80.MirrorCS")])]})])],"derivedFrom":makeQuery(id+"F3.opExtrude","CAP_EDGE",EDGE,{"disambiguationData":[OSD([subQ1,subQ0])],"isStart":true})});}
            var Q7;
            {var subQ0=sQuery(id+"F2.wireOp",EDGE,"E5.MirrorCS");var subQ1=sQuery(id+"F2.wireOp",EDGE,"E2");Q7=makeQuery(id+"F34.opChamfer","BLEND_EDGE",EDGE,{"blendedFrom":[makeQuery(id+"F31.opExtrude","CAP_EDGE",EDGE,{"disambiguationData":[OSD([sQuery(id+"F30.wireOp",EDGE,"E86.MirrorCS")])],"isStart":false}),makeQuery(id+"F31.boolean.opBoolean","MERGE",FACE,{"derivedFrom":[makeQuery(id+"F7.boolean.opBoolean","MERGE",FACE,{"derivedFrom":[makeQuery(id+"F5.boolean.opBoolean","MERGE",FACE,{"derivedFrom":[makeQuery(id+"F3.opExtrude","SWEPT_FACE",FACE,{"disambiguationData":[OSD([subQ1,subQ0])]}),makeQuery(id+"F5.opExtrude","SWEPT_FACE",FACE,{"disambiguationData":[OSD([sQuery(id+"F4.wireOp",EDGE,"E9")])]}),makeQuery(id+"F5.opExtrude","SWEPT_FACE",FACE,{"disambiguationData":[OSD([sQuery(id+"F4.wireOp",EDGE,"E11.MirrorCS")])]})]}),makeQuery(id+"F7.opExtrude","CAP_FACE",FACE,{"disambiguationData":[OSD([sQuery(id+"F6.wireOp",EDGE,"E16"),sQuery(id+"F6.wireOp",EDGE,"E17")])],"isStart":true}),makeQuery(id+"F7.opExtrude","CAP_FACE",FACE,{"disambiguationData":[OSD([subQ1,subQ0,sQuery(id+"F6.wireOp",EDGE,"E18.1.0.0")])],"isStart":true}),makeQuery(id+"F7.opExtrude","CAP_FACE",FACE,{"disambiguationData":[OSD([subQ1,subQ0,sQuery(id+"F6.wireOp",EDGE,"E18.2.0.0")])],"isStart":true}),makeQuery(id+"F7.opExtrude","CAP_FACE",FACE,{"disambiguationData":[OSD([subQ1,subQ0,sQuery(id+"F6.wireOp",EDGE,"E18.3.0.0")])],"isStart":true}),makeQuery(id+"F7.opExtrude","CAP_FACE",FACE,{"disambiguationData":[OSD([subQ1,subQ0,sQuery(id+"F6.wireOp",EDGE,"E18.4.0.0")])],"isStart":true}),makeQuery(id+"F7.opExtrude","CAP_FACE",FACE,{"disambiguationData":[OSD([subQ1,subQ0,sQuery(id+"F6.wireOp",EDGE,"E18.5.0.0")])],"isStart":true}),makeQuery(id+"F7.opExtrude","CAP_FACE",FACE,{"disambiguationData":[OSD([subQ1,subQ0,sQuery(id+"F6.wireOp",EDGE,"E18.6.0.0")])],"isStart":true}),makeQuery(id+"F7.opExtrude","CAP_FACE",FACE,{"disambiguationData":[OSD([subQ1,subQ0,sQuery(id+"F6.wireOp",EDGE,"E18.7.0.0")])],"isStart":true}),makeQuery(id+"F7.opExtrude","CAP_FACE",FACE,{"disambiguationData":[OSD([subQ1,subQ0,sQuery(id+"F6.wireOp",EDGE,"E18.8.0.0")])],"isStart":true}),makeQuery(id+"F7.opExtrude","CAP_FACE",FACE,{"disambiguationData":[OSD([subQ1,subQ0,sQuery(id+"F6.wireOp",EDGE,"E18.9.0.0")])],"isStart":true})]}),makeQuery(id+"F31.opExtrude","SWEPT_FACE",FACE,{"disambiguationData":[OSD([sQuery(id+"F30.wireOp",EDGE,"LmbyR1he-35kO-f53Q-696j-YAIKVnODTwI9")])]}),makeQuery(id+"F31.opExtrude","SWEPT_FACE",FACE,{"disambiguationData":[OSD([sQuery(id+"F30.wireOp",EDGE,"lc0urJVt-xGFD-1UqV-AUzd-Ddt8hkDyLtwQ"),sQuery(id+"F30.wireOp",EDGE,"9e28845e-500e-4894-8802-eb7ad12137a13.MirrorCS")])]}),makeQuery(id+"F31.opExtrude","SWEPT_FACE",FACE,{"disambiguationData":[OSD([sQuery(id+"F30.wireOp",EDGE,"9e28845e-500e-4894-8802-eb7ad12137a10.MirrorCS")])]})]})],"blendedInto":[makeQuery(id+"F31.boolean.opBoolean","MERGE",FACE,{"derivedFrom":[makeQuery(id+"F7.boolean.opBoolean","MERGE",FACE,{"derivedFrom":[makeQuery(id+"F5.boolean.opBoolean","MERGE",FACE,{"derivedFrom":[makeQuery(id+"F3.opExtrude","SWEPT_FACE",FACE,{"disambiguationData":[OSD([subQ1,subQ0])]}),makeQuery(id+"F5.opExtrude","SWEPT_FACE",FACE,{"disambiguationData":[OSD([sQuery(id+"F4.wireOp",EDGE,"E9")])]}),makeQuery(id+"F5.opExtrude","SWEPT_FACE",FACE,{"disambiguationData":[OSD([sQuery(id+"F4.wireOp",EDGE,"E11.MirrorCS")])]})]}),makeQuery(id+"F7.opExtrude","CAP_FACE",FACE,{"disambiguationData":[OSD([sQuery(id+"F6.wireOp",EDGE,"E16"),sQuery(id+"F6.wireOp",EDGE,"E17")])],"isStart":true}),makeQuery(id+"F7.opExtrude","CAP_FACE",FACE,{"disambiguationData":[OSD([subQ1,subQ0,sQuery(id+"F6.wireOp",EDGE,"E18.1.0.0")])],"isStart":true}),makeQuery(id+"F7.opExtrude","CAP_FACE",FACE,{"disambiguationData":[OSD([subQ1,subQ0,sQuery(id+"F6.wireOp",EDGE,"E18.2.0.0")])],"isStart":true}),makeQuery(id+"F7.opExtrude","CAP_FACE",FACE,{"disambiguationData":[OSD([subQ1,subQ0,sQuery(id+"F6.wireOp",EDGE,"E18.3.0.0")])],"isStart":true}),makeQuery(id+"F7.opExtrude","CAP_FACE",FACE,{"disambiguationData":[OSD([subQ1,subQ0,sQuery(id+"F6.wireOp",EDGE,"E18.4.0.0")])],"isStart":true}),makeQuery(id+"F7.opExtrude","CAP_FACE",FACE,{"disambiguationData":[OSD([subQ1,subQ0,sQuery(id+"F6.wireOp",EDGE,"E18.5.0.0")])],"isStart":true}),makeQuery(id+"F7.opExtrude","CAP_FACE",FACE,{"disambiguationData":[OSD([subQ1,subQ0,sQuery(id+"F6.wireOp",EDGE,"E18.6.0.0")])],"isStart":true}),makeQuery(id+"F7.opExtrude","CAP_FACE",FACE,{"disambiguationData":[OSD([subQ1,subQ0,sQuery(id+"F6.wireOp",EDGE,"E18.7.0.0")])],"isStart":true}),makeQuery(id+"F7.opExtrude","CAP_FACE",FACE,{"disambiguationData":[OSD([subQ1,subQ0,sQuery(id+"F6.wireOp",EDGE,"E18.8.0.0")])],"isStart":true}),makeQuery(id+"F7.opExtrude","CAP_FACE",FACE,{"disambiguationData":[OSD([subQ1,subQ0,sQuery(id+"F6.wireOp",EDGE,"E18.9.0.0")])],"isStart":true})]}),makeQuery(id+"F31.opExtrude","SWEPT_FACE",FACE,{"disambiguationData":[OSD([sQuery(id+"F30.wireOp",EDGE,"LmbyR1he-35kO-f53Q-696j-YAIKVnODTwI9")])]}),makeQuery(id+"F31.opExtrude","SWEPT_FACE",FACE,{"disambiguationData":[OSD([sQuery(id+"F30.wireOp",EDGE,"lc0urJVt-xGFD-1UqV-AUzd-Ddt8hkDyLtwQ"),sQuery(id+"F30.wireOp",EDGE,"9e28845e-500e-4894-8802-eb7ad12137a13.MirrorCS")])]}),makeQuery(id+"F31.opExtrude","SWEPT_FACE",FACE,{"disambiguationData":[OSD([sQuery(id+"F30.wireOp",EDGE,"9e28845e-500e-4894-8802-eb7ad12137a10.MirrorCS")])]})]})]});}
            var Q8;
            Q8=makeQuery(id+"F31.opExtrude","CAP_EDGE",EDGE,{"disambiguationData":[OSD([sQuery(id+"F30.wireOp",EDGE,"9e28845e-500e-4894-8802-eb7ad12137a10.MirrorCS")])],"isStart":false});
            var Q9;
            {var subQ0=sQuery(id+"F2.wireOp",EDGE,"E5.MirrorCS");var subQ1=sQuery(id+"F2.wireOp",EDGE,"E2");Q9=makeQuery(id+"F34.opChamfer","BLEND_EDGE",EDGE,{"blendedFrom":[makeQuery(id+"F31.opExtrude","CAP_EDGE",EDGE,{"disambiguationData":[OSD([sQuery(id+"F30.wireOp",EDGE,"E74")])],"isStart":false}),makeQuery(id+"F31.boolean.opBoolean","MERGE",FACE,{"derivedFrom":[makeQuery(id+"F7.boolean.opBoolean","MERGE",FACE,{"derivedFrom":[makeQuery(id+"F5.boolean.opBoolean","MERGE",FACE,{"derivedFrom":[makeQuery(id+"F3.opExtrude","SWEPT_FACE",FACE,{"disambiguationData":[OSD([subQ1,subQ0])]}),makeQuery(id+"F5.opExtrude","SWEPT_FACE",FACE,{"disambiguationData":[OSD([sQuery(id+"F4.wireOp",EDGE,"E9")])]}),makeQuery(id+"F5.opExtrude","SWEPT_FACE",FACE,{"disambiguationData":[OSD([sQuery(id+"F4.wireOp",EDGE,"E11.MirrorCS")])]})]}),makeQuery(id+"F7.opExtrude","CAP_FACE",FACE,{"disambiguationData":[OSD([sQuery(id+"F6.wireOp",EDGE,"E16"),sQuery(id+"F6.wireOp",EDGE,"E17")])],"isStart":true}),makeQuery(id+"F7.opExtrude","CAP_FACE",FACE,{"disambiguationData":[OSD([subQ1,subQ0,sQuery(id+"F6.wireOp",EDGE,"E18.1.0.0")])],"isStart":true}),makeQuery(id+"F7.opExtrude","CAP_FACE",FACE,{"disambiguationData":[OSD([subQ1,subQ0,sQuery(id+"F6.wireOp",EDGE,"E18.2.0.0")])],"isStart":true}),makeQuery(id+"F7.opExtrude","CAP_FACE",FACE,{"disambiguationData":[OSD([subQ1,subQ0,sQuery(id+"F6.wireOp",EDGE,"E18.3.0.0")])],"isStart":true}),makeQuery(id+"F7.opExtrude","CAP_FACE",FACE,{"disambiguationData":[OSD([subQ1,subQ0,sQuery(id+"F6.wireOp",EDGE,"E18.4.0.0")])],"isStart":true}),makeQuery(id+"F7.opExtrude","CAP_FACE",FACE,{"disambiguationData":[OSD([subQ1,subQ0,sQuery(id+"F6.wireOp",EDGE,"E18.5.0.0")])],"isStart":true}),makeQuery(id+"F7.opExtrude","CAP_FACE",FACE,{"disambiguationData":[OSD([subQ1,subQ0,sQuery(id+"F6.wireOp",EDGE,"E18.6.0.0")])],"isStart":true}),makeQuery(id+"F7.opExtrude","CAP_FACE",FACE,{"disambiguationData":[OSD([subQ1,subQ0,sQuery(id+"F6.wireOp",EDGE,"E18.7.0.0")])],"isStart":true}),makeQuery(id+"F7.opExtrude","CAP_FACE",FACE,{"disambiguationData":[OSD([subQ1,subQ0,sQuery(id+"F6.wireOp",EDGE,"E18.8.0.0")])],"isStart":true}),makeQuery(id+"F7.opExtrude","CAP_FACE",FACE,{"disambiguationData":[OSD([subQ1,subQ0,sQuery(id+"F6.wireOp",EDGE,"E18.9.0.0")])],"isStart":true})]}),makeQuery(id+"F31.opExtrude","SWEPT_FACE",FACE,{"disambiguationData":[OSD([sQuery(id+"F30.wireOp",EDGE,"LmbyR1he-35kO-f53Q-696j-YAIKVnODTwI9")])]}),makeQuery(id+"F31.opExtrude","SWEPT_FACE",FACE,{"disambiguationData":[OSD([sQuery(id+"F30.wireOp",EDGE,"lc0urJVt-xGFD-1UqV-AUzd-Ddt8hkDyLtwQ"),sQuery(id+"F30.wireOp",EDGE,"9e28845e-500e-4894-8802-eb7ad12137a13.MirrorCS")])]}),makeQuery(id+"F31.opExtrude","SWEPT_FACE",FACE,{"disambiguationData":[OSD([sQuery(id+"F30.wireOp",EDGE,"9e28845e-500e-4894-8802-eb7ad12137a10.MirrorCS")])]})]})],"blendedInto":[makeQuery(id+"F31.boolean.opBoolean","MERGE",FACE,{"derivedFrom":[makeQuery(id+"F7.boolean.opBoolean","MERGE",FACE,{"derivedFrom":[makeQuery(id+"F5.boolean.opBoolean","MERGE",FACE,{"derivedFrom":[makeQuery(id+"F3.opExtrude","SWEPT_FACE",FACE,{"disambiguationData":[OSD([subQ1,subQ0])]}),makeQuery(id+"F5.opExtrude","SWEPT_FACE",FACE,{"disambiguationData":[OSD([sQuery(id+"F4.wireOp",EDGE,"E9")])]}),makeQuery(id+"F5.opExtrude","SWEPT_FACE",FACE,{"disambiguationData":[OSD([sQuery(id+"F4.wireOp",EDGE,"E11.MirrorCS")])]})]}),makeQuery(id+"F7.opExtrude","CAP_FACE",FACE,{"disambiguationData":[OSD([sQuery(id+"F6.wireOp",EDGE,"E16"),sQuery(id+"F6.wireOp",EDGE,"E17")])],"isStart":true}),makeQuery(id+"F7.opExtrude","CAP_FACE",FACE,{"disambiguationData":[OSD([subQ1,subQ0,sQuery(id+"F6.wireOp",EDGE,"E18.1.0.0")])],"isStart":true}),makeQuery(id+"F7.opExtrude","CAP_FACE",FACE,{"disambiguationData":[OSD([subQ1,subQ0,sQuery(id+"F6.wireOp",EDGE,"E18.2.0.0")])],"isStart":true}),makeQuery(id+"F7.opExtrude","CAP_FACE",FACE,{"disambiguationData":[OSD([subQ1,subQ0,sQuery(id+"F6.wireOp",EDGE,"E18.3.0.0")])],"isStart":true}),makeQuery(id+"F7.opExtrude","CAP_FACE",FACE,{"disambiguationData":[OSD([subQ1,subQ0,sQuery(id+"F6.wireOp",EDGE,"E18.4.0.0")])],"isStart":true}),makeQuery(id+"F7.opExtrude","CAP_FACE",FACE,{"disambiguationData":[OSD([subQ1,subQ0,sQuery(id+"F6.wireOp",EDGE,"E18.5.0.0")])],"isStart":true}),makeQuery(id+"F7.opExtrude","CAP_FACE",FACE,{"disambiguationData":[OSD([subQ1,subQ0,sQuery(id+"F6.wireOp",EDGE,"E18.6.0.0")])],"isStart":true}),makeQuery(id+"F7.opExtrude","CAP_FACE",FACE,{"disambiguationData":[OSD([subQ1,subQ0,sQuery(id+"F6.wireOp",EDGE,"E18.7.0.0")])],"isStart":true}),makeQuery(id+"F7.opExtrude","CAP_FACE",FACE,{"disambiguationData":[OSD([subQ1,subQ0,sQuery(id+"F6.wireOp",EDGE,"E18.8.0.0")])],"isStart":true}),makeQuery(id+"F7.opExtrude","CAP_FACE",FACE,{"disambiguationData":[OSD([subQ1,subQ0,sQuery(id+"F6.wireOp",EDGE,"E18.9.0.0")])],"isStart":true})]}),makeQuery(id+"F31.opExtrude","SWEPT_FACE",FACE,{"disambiguationData":[OSD([sQuery(id+"F30.wireOp",EDGE,"LmbyR1he-35kO-f53Q-696j-YAIKVnODTwI9")])]}),makeQuery(id+"F31.opExtrude","SWEPT_FACE",FACE,{"disambiguationData":[OSD([sQuery(id+"F30.wireOp",EDGE,"lc0urJVt-xGFD-1UqV-AUzd-Ddt8hkDyLtwQ"),sQuery(id+"F30.wireOp",EDGE,"9e28845e-500e-4894-8802-eb7ad12137a13.MirrorCS")])]}),makeQuery(id+"F31.opExtrude","SWEPT_FACE",FACE,{"disambiguationData":[OSD([sQuery(id+"F30.wireOp",EDGE,"9e28845e-500e-4894-8802-eb7ad12137a10.MirrorCS")])]})]})]});}
            var Q10;
            Q10=makeQuery(id+"F31.boolean.opBoolean","MERGE",EDGE,{"derivedFrom":[makeQuery(id+"F5.boolean.opBoolean","MERGE",EDGE,{"derivedFrom":[makeQuery(id+"F3.opExtrude","SWEPT_EDGE",EDGE,{"disambiguationData":[OSD([sQuery(id+"F2.wireOp",EDGE,"E1"),sQuery(id+"F2.wireOp",EDGE,"E2")])]}),makeQuery(id+"F5.opExtrude","SWEPT_EDGE",EDGE,{"disambiguationData":[OSD([sQuery(id+"F4.wireOp",EDGE,"E7"),sQuery(id+"F4.wireOp",EDGE,"E9")])]})]}),makeQuery(id+"F31.opExtrude","SWEPT_EDGE",EDGE,{"disambiguationData":[OSD([sQuery(id+"F30.wireOp",EDGE,"E74"),sQuery(id+"F30.wireOp",EDGE,"LmbyR1he-35kO-f53Q-696j-YAIKVnODTwI9")])]})]});
            var Q11;
            Q11=makeQuery(id+"F5.opExtrude","CAP_EDGE",EDGE,{"disambiguationData":[OSD([sQuery(id+"F4.wireOp",EDGE,"E9")])],"isStart":false});
            var Q12;
            Q12=makeQuery(id+"F5.opExtrude","SWEPT_EDGE",EDGE,{"disambiguationData":[OSD([sQuery(id+"F2.wireOp",EDGE,"E2"),sQuery(id+"F2.wireOp",EDGE,"E5.MirrorCS"),sQuery(id+"F4.wireOp",EDGE,"E8"),sQuery(id+"F4.wireOp",EDGE,"E9")])]});
            var Q13;
            {var subQ0=sQuery(id+"F2.wireOp",EDGE,"E5.MirrorCS");var subQ1=sQuery(id+"F2.wireOp",EDGE,"E2");Q13=makeQuery(id+"F34.opChamfer","BLEND_EDGE",EDGE,{"blendedFrom":[makeQuery(id+"F31.opExtrude","CAP_EDGE",EDGE,{"disambiguationData":[OSD([sQuery(id+"F30.wireOp",EDGE,"E78.MirrorCS")])],"isStart":false}),makeQuery(id+"F31.boolean.opBoolean","MERGE",FACE,{"derivedFrom":[makeQuery(id+"F7.boolean.opBoolean","MERGE",FACE,{"derivedFrom":[makeQuery(id+"F5.boolean.opBoolean","MERGE",FACE,{"derivedFrom":[makeQuery(id+"F3.opExtrude","SWEPT_FACE",FACE,{"disambiguationData":[OSD([subQ1,subQ0])]}),makeQuery(id+"F5.opExtrude","SWEPT_FACE",FACE,{"disambiguationData":[OSD([sQuery(id+"F4.wireOp",EDGE,"E9")])]}),makeQuery(id+"F5.opExtrude","SWEPT_FACE",FACE,{"disambiguationData":[OSD([sQuery(id+"F4.wireOp",EDGE,"E11.MirrorCS")])]})]}),makeQuery(id+"F7.opExtrude","CAP_FACE",FACE,{"disambiguationData":[OSD([sQuery(id+"F6.wireOp",EDGE,"E16"),sQuery(id+"F6.wireOp",EDGE,"E17")])],"isStart":true}),makeQuery(id+"F7.opExtrude","CAP_FACE",FACE,{"disambiguationData":[OSD([subQ1,subQ0,sQuery(id+"F6.wireOp",EDGE,"E18.1.0.0")])],"isStart":true}),makeQuery(id+"F7.opExtrude","CAP_FACE",FACE,{"disambiguationData":[OSD([subQ1,subQ0,sQuery(id+"F6.wireOp",EDGE,"E18.2.0.0")])],"isStart":true}),makeQuery(id+"F7.opExtrude","CAP_FACE",FACE,{"disambiguationData":[OSD([subQ1,subQ0,sQuery(id+"F6.wireOp",EDGE,"E18.3.0.0")])],"isStart":true}),makeQuery(id+"F7.opExtrude","CAP_FACE",FACE,{"disambiguationData":[OSD([subQ1,subQ0,sQuery(id+"F6.wireOp",EDGE,"E18.4.0.0")])],"isStart":true}),makeQuery(id+"F7.opExtrude","CAP_FACE",FACE,{"disambiguationData":[OSD([subQ1,subQ0,sQuery(id+"F6.wireOp",EDGE,"E18.5.0.0")])],"isStart":true}),makeQuery(id+"F7.opExtrude","CAP_FACE",FACE,{"disambiguationData":[OSD([subQ1,subQ0,sQuery(id+"F6.wireOp",EDGE,"E18.6.0.0")])],"isStart":true}),makeQuery(id+"F7.opExtrude","CAP_FACE",FACE,{"disambiguationData":[OSD([subQ1,subQ0,sQuery(id+"F6.wireOp",EDGE,"E18.7.0.0")])],"isStart":true}),makeQuery(id+"F7.opExtrude","CAP_FACE",FACE,{"disambiguationData":[OSD([subQ1,subQ0,sQuery(id+"F6.wireOp",EDGE,"E18.8.0.0")])],"isStart":true}),makeQuery(id+"F7.opExtrude","CAP_FACE",FACE,{"disambiguationData":[OSD([subQ1,subQ0,sQuery(id+"F6.wireOp",EDGE,"E18.9.0.0")])],"isStart":true})]}),makeQuery(id+"F31.opExtrude","SWEPT_FACE",FACE,{"disambiguationData":[OSD([sQuery(id+"F30.wireOp",EDGE,"LmbyR1he-35kO-f53Q-696j-YAIKVnODTwI9")])]}),makeQuery(id+"F31.opExtrude","SWEPT_FACE",FACE,{"disambiguationData":[OSD([sQuery(id+"F30.wireOp",EDGE,"lc0urJVt-xGFD-1UqV-AUzd-Ddt8hkDyLtwQ"),sQuery(id+"F30.wireOp",EDGE,"9e28845e-500e-4894-8802-eb7ad12137a13.MirrorCS")])]}),makeQuery(id+"F31.opExtrude","SWEPT_FACE",FACE,{"disambiguationData":[OSD([sQuery(id+"F30.wireOp",EDGE,"9e28845e-500e-4894-8802-eb7ad12137a10.MirrorCS")])]})]})],"blendedInto":[makeQuery(id+"F31.boolean.opBoolean","MERGE",FACE,{"derivedFrom":[makeQuery(id+"F7.boolean.opBoolean","MERGE",FACE,{"derivedFrom":[makeQuery(id+"F5.boolean.opBoolean","MERGE",FACE,{"derivedFrom":[makeQuery(id+"F3.opExtrude","SWEPT_FACE",FACE,{"disambiguationData":[OSD([subQ1,subQ0])]}),makeQuery(id+"F5.opExtrude","SWEPT_FACE",FACE,{"disambiguationData":[OSD([sQuery(id+"F4.wireOp",EDGE,"E9")])]}),makeQuery(id+"F5.opExtrude","SWEPT_FACE",FACE,{"disambiguationData":[OSD([sQuery(id+"F4.wireOp",EDGE,"E11.MirrorCS")])]})]}),makeQuery(id+"F7.opExtrude","CAP_FACE",FACE,{"disambiguationData":[OSD([sQuery(id+"F6.wireOp",EDGE,"E16"),sQuery(id+"F6.wireOp",EDGE,"E17")])],"isStart":true}),makeQuery(id+"F7.opExtrude","CAP_FACE",FACE,{"disambiguationData":[OSD([subQ1,subQ0,sQuery(id+"F6.wireOp",EDGE,"E18.1.0.0")])],"isStart":true}),makeQuery(id+"F7.opExtrude","CAP_FACE",FACE,{"disambiguationData":[OSD([subQ1,subQ0,sQuery(id+"F6.wireOp",EDGE,"E18.2.0.0")])],"isStart":true}),makeQuery(id+"F7.opExtrude","CAP_FACE",FACE,{"disambiguationData":[OSD([subQ1,subQ0,sQuery(id+"F6.wireOp",EDGE,"E18.3.0.0")])],"isStart":true}),makeQuery(id+"F7.opExtrude","CAP_FACE",FACE,{"disambiguationData":[OSD([subQ1,subQ0,sQuery(id+"F6.wireOp",EDGE,"E18.4.0.0")])],"isStart":true}),makeQuery(id+"F7.opExtrude","CAP_FACE",FACE,{"disambiguationData":[OSD([subQ1,subQ0,sQuery(id+"F6.wireOp",EDGE,"E18.5.0.0")])],"isStart":true}),makeQuery(id+"F7.opExtrude","CAP_FACE",FACE,{"disambiguationData":[OSD([subQ1,subQ0,sQuery(id+"F6.wireOp",EDGE,"E18.6.0.0")])],"isStart":true}),makeQuery(id+"F7.opExtrude","CAP_FACE",FACE,{"disambiguationData":[OSD([subQ1,subQ0,sQuery(id+"F6.wireOp",EDGE,"E18.7.0.0")])],"isStart":true}),makeQuery(id+"F7.opExtrude","CAP_FACE",FACE,{"disambiguationData":[OSD([subQ1,subQ0,sQuery(id+"F6.wireOp",EDGE,"E18.8.0.0")])],"isStart":true}),makeQuery(id+"F7.opExtrude","CAP_FACE",FACE,{"disambiguationData":[OSD([subQ1,subQ0,sQuery(id+"F6.wireOp",EDGE,"E18.9.0.0")])],"isStart":true})]}),makeQuery(id+"F31.opExtrude","SWEPT_FACE",FACE,{"disambiguationData":[OSD([sQuery(id+"F30.wireOp",EDGE,"LmbyR1he-35kO-f53Q-696j-YAIKVnODTwI9")])]}),makeQuery(id+"F31.opExtrude","SWEPT_FACE",FACE,{"disambiguationData":[OSD([sQuery(id+"F30.wireOp",EDGE,"lc0urJVt-xGFD-1UqV-AUzd-Ddt8hkDyLtwQ"),sQuery(id+"F30.wireOp",EDGE,"9e28845e-500e-4894-8802-eb7ad12137a13.MirrorCS")])]}),makeQuery(id+"F31.opExtrude","SWEPT_FACE",FACE,{"disambiguationData":[OSD([sQuery(id+"F30.wireOp",EDGE,"9e28845e-500e-4894-8802-eb7ad12137a10.MirrorCS")])]})]})]});}
            var Q14;
            Q14=makeQuery(id+"F31.boolean.opBoolean","MERGE",EDGE,{"derivedFrom":[makeQuery(id+"F5.boolean.opBoolean","MERGE",EDGE,{"derivedFrom":[makeQuery(id+"F3.opExtrude","SWEPT_EDGE",EDGE,{"disambiguationData":[OSD([sQuery(id+"F2.wireOp",EDGE,"E4.MirrorCS"),sQuery(id+"F2.wireOp",EDGE,"E5.MirrorCS")])]}),makeQuery(id+"F5.opExtrude","SWEPT_EDGE",EDGE,{"disambiguationData":[OSD([sQuery(id+"F4.wireOp",EDGE,"E11.MirrorCS"),sQuery(id+"F4.wireOp",EDGE,"E12.MirrorCS")])]})]}),makeQuery(id+"F31.opExtrude","SWEPT_EDGE",EDGE,{"disambiguationData":[OSD([sQuery(id+"F30.wireOp",EDGE,"9e28845e-500e-4894-8802-eb7ad12137a10.MirrorCS"),sQuery(id+"F30.wireOp",EDGE,"E78.MirrorCS")])]})]});
            var Q15;
            Q15=makeQuery(id+"F5.opExtrude","CAP_EDGE",EDGE,{"disambiguationData":[OSD([sQuery(id+"F4.wireOp",EDGE,"E11.MirrorCS")])],"isStart":false});
            var Q16;
            Q16=makeQuery(id+"F5.opExtrude","SWEPT_EDGE",EDGE,{"disambiguationData":[OSD([sQuery(id+"F2.wireOp",EDGE,"E2"),sQuery(id+"F2.wireOp",EDGE,"E5.MirrorCS"),sQuery(id+"F4.wireOp",EDGE,"E10.MirrorCS"),sQuery(id+"F4.wireOp",EDGE,"E11.MirrorCS")])]});
            var Q17;
            Q17=makeQuery(id+"F5.opExtrude","CAP_EDGE",EDGE,{"disambiguationData":[OSD([sQuery(id+"F4.wireOp",EDGE,"E12.MirrorCS")])],"isStart":false});
            var Q18;
            Q18=makeQuery(id+"F5.opExtrude","CAP_EDGE",EDGE,{"disambiguationData":[OSD([sQuery(id+"F4.wireOp",EDGE,"E10.MirrorCS")])],"isStart":false});
            var Q19;
            Q19=makeQuery(id+"F5.opExtrude","CAP_EDGE",EDGE,{"disambiguationData":[OSD([sQuery(id+"F4.wireOp",EDGE,"E14")])],"isStart":false});
            var Q20;
            Q20=makeQuery(id+"F5.opExtrude","CAP_EDGE",EDGE,{"disambiguationData":[OSD([sQuery(id+"F4.wireOp",EDGE,"E8")])],"isStart":false});
            var Q21;
            {var subQ0=sQuery(id+"F2.wireOp",EDGE,"E3.MirrorCS");var subQ1=sQuery(id+"F2.wireOp",EDGE,"E0");var subQ2=sQuery(id+"F2.wireOp",EDGE,"E4.MirrorCS");Q21=makeQuery(id+"F13.boolean.opBoolean","SPLIT",EDGE,{"disambiguationData":[TD([makeQuery(id+"F3.opExtrude","SWEPT_FACE",FACE,{"disambiguationData":[OSD([subQ2])]})])],"derivedFrom":makeQuery(id+"F3.opExtrude","CAP_EDGE",EDGE,{"disambiguationData":[OSD([subQ1,subQ0])],"isStart":true})});}
            var Q22;
            {var subQ0=sQuery(id+"F2.wireOp",EDGE,"E1");var subQ1=sQuery(id+"F2.wireOp",EDGE,"E3.MirrorCS");var subQ2=sQuery(id+"F2.wireOp",EDGE,"E0");Q22=makeQuery(id+"F13.boolean.opBoolean","SPLIT",EDGE,{"disambiguationData":[TD([makeQuery(id+"F3.opExtrude","SWEPT_FACE",FACE,{"disambiguationData":[OSD([subQ0])]})])],"derivedFrom":makeQuery(id+"F3.opExtrude","CAP_EDGE",EDGE,{"disambiguationData":[OSD([subQ2,subQ1])],"isStart":true})});}
            var Q23;
            Q23=makeQuery(id+"F25.boolean.opBoolean","INTERSECT",EDGE,{"derivedFrom":[makeQuery(id+"F5.opExtrude","SWEPT_FACE",FACE,{"disambiguationData":[OSD([sQuery(id+"F4.wireOp",EDGE,"E14")])]}),makeQuery(id+"F25.opExtrude","SWEPT_FACE",FACE,{"disambiguationData":[OSD([sQuery(id+"F24.wireOp",EDGE,"E60")])]})]});
            var Q24;
            {var subQ0=sQuery(id+"F2.wireOp",EDGE,"E5.MirrorCS");var subQ1=sQuery(id+"F2.wireOp",EDGE,"E2");Q24=makeQuery(id+"F34.opChamfer","BLEND_EDGE",EDGE,{"blendedFrom":[makeQuery(id+"F31.opExtrude","CAP_EDGE",EDGE,{"disambiguationData":[OSD([sQuery(id+"F30.wireOp",EDGE,"E93")])],"isStart":false}),makeQuery(id+"F31.boolean.opBoolean","MERGE",FACE,{"derivedFrom":[makeQuery(id+"F7.boolean.opBoolean","MERGE",FACE,{"derivedFrom":[makeQuery(id+"F5.boolean.opBoolean","MERGE",FACE,{"derivedFrom":[makeQuery(id+"F3.opExtrude","SWEPT_FACE",FACE,{"disambiguationData":[OSD([subQ1,subQ0])]}),makeQuery(id+"F5.opExtrude","SWEPT_FACE",FACE,{"disambiguationData":[OSD([sQuery(id+"F4.wireOp",EDGE,"E9")])]}),makeQuery(id+"F5.opExtrude","SWEPT_FACE",FACE,{"disambiguationData":[OSD([sQuery(id+"F4.wireOp",EDGE,"E11.MirrorCS")])]})]}),makeQuery(id+"F7.opExtrude","CAP_FACE",FACE,{"disambiguationData":[OSD([sQuery(id+"F6.wireOp",EDGE,"E16"),sQuery(id+"F6.wireOp",EDGE,"E17")])],"isStart":true}),makeQuery(id+"F7.opExtrude","CAP_FACE",FACE,{"disambiguationData":[OSD([subQ1,subQ0,sQuery(id+"F6.wireOp",EDGE,"E18.1.0.0")])],"isStart":true}),makeQuery(id+"F7.opExtrude","CAP_FACE",FACE,{"disambiguationData":[OSD([subQ1,subQ0,sQuery(id+"F6.wireOp",EDGE,"E18.2.0.0")])],"isStart":true}),makeQuery(id+"F7.opExtrude","CAP_FACE",FACE,{"disambiguationData":[OSD([subQ1,subQ0,sQuery(id+"F6.wireOp",EDGE,"E18.3.0.0")])],"isStart":true}),makeQuery(id+"F7.opExtrude","CAP_FACE",FACE,{"disambiguationData":[OSD([subQ1,subQ0,sQuery(id+"F6.wireOp",EDGE,"E18.4.0.0")])],"isStart":true}),makeQuery(id+"F7.opExtrude","CAP_FACE",FACE,{"disambiguationData":[OSD([subQ1,subQ0,sQuery(id+"F6.wireOp",EDGE,"E18.5.0.0")])],"isStart":true}),makeQuery(id+"F7.opExtrude","CAP_FACE",FACE,{"disambiguationData":[OSD([subQ1,subQ0,sQuery(id+"F6.wireOp",EDGE,"E18.6.0.0")])],"isStart":true}),makeQuery(id+"F7.opExtrude","CAP_FACE",FACE,{"disambiguationData":[OSD([subQ1,subQ0,sQuery(id+"F6.wireOp",EDGE,"E18.7.0.0")])],"isStart":true})]}),makeQuery(id+"F31.opExtrude","SWEPT_FACE",FACE,{"disambiguationData":[OSD([sQuery(id+"F30.wireOp",EDGE,"E88")])]}),makeQuery(id+"F31.opExtrude","SWEPT_FACE",FACE,{"disambiguationData":[OSD([sQuery(id+"F30.wireOp",EDGE,"E89")])]}),makeQuery(id+"F31.opExtrude","SWEPT_FACE",FACE,{"disambiguationData":[OSD([sQuery(id+"F30.wireOp",EDGE,"E90")])]}),makeQuery(id+"F31.opExtrude","SWEPT_FACE",FACE,{"disambiguationData":[OSD([sQuery(id+"F30.wireOp",EDGE,"E94")])]})]})],"blendedInto":[makeQuery(id+"F31.boolean.opBoolean","MERGE",FACE,{"derivedFrom":[makeQuery(id+"F7.boolean.opBoolean","MERGE",FACE,{"derivedFrom":[makeQuery(id+"F5.boolean.opBoolean","MERGE",FACE,{"derivedFrom":[makeQuery(id+"F3.opExtrude","SWEPT_FACE",FACE,{"disambiguationData":[OSD([subQ1,subQ0])]}),makeQuery(id+"F5.opExtrude","SWEPT_FACE",FACE,{"disambiguationData":[OSD([sQuery(id+"F4.wireOp",EDGE,"E9")])]}),makeQuery(id+"F5.opExtrude","SWEPT_FACE",FACE,{"disambiguationData":[OSD([sQuery(id+"F4.wireOp",EDGE,"E11.MirrorCS")])]})]}),makeQuery(id+"F7.opExtrude","CAP_FACE",FACE,{"disambiguationData":[OSD([sQuery(id+"F6.wireOp",EDGE,"E16"),sQuery(id+"F6.wireOp",EDGE,"E17")])],"isStart":true}),makeQuery(id+"F7.opExtrude","CAP_FACE",FACE,{"disambiguationData":[OSD([subQ1,subQ0,sQuery(id+"F6.wireOp",EDGE,"E18.1.0.0")])],"isStart":true}),makeQuery(id+"F7.opExtrude","CAP_FACE",FACE,{"disambiguationData":[OSD([subQ1,subQ0,sQuery(id+"F6.wireOp",EDGE,"E18.2.0.0")])],"isStart":true}),makeQuery(id+"F7.opExtrude","CAP_FACE",FACE,{"disambiguationData":[OSD([subQ1,subQ0,sQuery(id+"F6.wireOp",EDGE,"E18.3.0.0")])],"isStart":true}),makeQuery(id+"F7.opExtrude","CAP_FACE",FACE,{"disambiguationData":[OSD([subQ1,subQ0,sQuery(id+"F6.wireOp",EDGE,"E18.4.0.0")])],"isStart":true}),makeQuery(id+"F7.opExtrude","CAP_FACE",FACE,{"disambiguationData":[OSD([subQ1,subQ0,sQuery(id+"F6.wireOp",EDGE,"E18.5.0.0")])],"isStart":true}),makeQuery(id+"F7.opExtrude","CAP_FACE",FACE,{"disambiguationData":[OSD([subQ1,subQ0,sQuery(id+"F6.wireOp",EDGE,"E18.6.0.0")])],"isStart":true}),makeQuery(id+"F7.opExtrude","CAP_FACE",FACE,{"disambiguationData":[OSD([subQ1,subQ0,sQuery(id+"F6.wireOp",EDGE,"E18.7.0.0")])],"isStart":true})]}),makeQuery(id+"F31.opExtrude","SWEPT_FACE",FACE,{"disambiguationData":[OSD([sQuery(id+"F30.wireOp",EDGE,"E88")])]}),makeQuery(id+"F31.opExtrude","SWEPT_FACE",FACE,{"disambiguationData":[OSD([sQuery(id+"F30.wireOp",EDGE,"E89")])]}),makeQuery(id+"F31.opExtrude","SWEPT_FACE",FACE,{"disambiguationData":[OSD([sQuery(id+"F30.wireOp",EDGE,"E90")])]}),makeQuery(id+"F31.opExtrude","SWEPT_FACE",FACE,{"disambiguationData":[OSD([sQuery(id+"F30.wireOp",EDGE,"E94")])]})]})]});}
            var Q25;
            {var subQ0=sQuery(id+"F2.wireOp",EDGE,"E5.MirrorCS");var subQ1=sQuery(id+"F2.wireOp",EDGE,"E2");Q25=makeQuery(id+"F31.boolean.opBoolean","SPLIT",EDGE,{"disambiguationData":[TD([makeQuery(id+"F31.opExtrude","SWEPT_FACE",FACE,{"disambiguationData":[OSD([sQuery(id+"F30.wireOp",EDGE,"E91")])]})])],"derivedFrom":makeQuery(id+"F3.opExtrude","CAP_EDGE",EDGE,{"disambiguationData":[OSD([subQ1,subQ0])],"isStart":true})});}
            var Q26;
            {var subQ0=sQuery(id+"F2.wireOp",EDGE,"E5.MirrorCS");var subQ1=sQuery(id+"F2.wireOp",EDGE,"E2");Q26=makeQuery(id+"F34.opChamfer","BLEND_EDGE",EDGE,{"blendedFrom":[makeQuery(id+"F31.opExtrude","CAP_EDGE",EDGE,{"disambiguationData":[OSD([sQuery(id+"F30.wireOp",EDGE,"E91")])],"isStart":false}),makeQuery(id+"F31.boolean.opBoolean","MERGE",FACE,{"derivedFrom":[makeQuery(id+"F7.boolean.opBoolean","MERGE",FACE,{"derivedFrom":[makeQuery(id+"F5.boolean.opBoolean","MERGE",FACE,{"derivedFrom":[makeQuery(id+"F3.opExtrude","SWEPT_FACE",FACE,{"disambiguationData":[OSD([subQ1,subQ0])]}),makeQuery(id+"F5.opExtrude","SWEPT_FACE",FACE,{"disambiguationData":[OSD([sQuery(id+"F4.wireOp",EDGE,"E9")])]}),makeQuery(id+"F5.opExtrude","SWEPT_FACE",FACE,{"disambiguationData":[OSD([sQuery(id+"F4.wireOp",EDGE,"E11.MirrorCS")])]})]}),makeQuery(id+"F7.opExtrude","CAP_FACE",FACE,{"disambiguationData":[OSD([sQuery(id+"F6.wireOp",EDGE,"E16"),sQuery(id+"F6.wireOp",EDGE,"E17")])],"isStart":true}),makeQuery(id+"F7.opExtrude","CAP_FACE",FACE,{"disambiguationData":[OSD([subQ1,subQ0,sQuery(id+"F6.wireOp",EDGE,"E18.1.0.0")])],"isStart":true}),makeQuery(id+"F7.opExtrude","CAP_FACE",FACE,{"disambiguationData":[OSD([subQ1,subQ0,sQuery(id+"F6.wireOp",EDGE,"E18.2.0.0")])],"isStart":true}),makeQuery(id+"F7.opExtrude","CAP_FACE",FACE,{"disambiguationData":[OSD([subQ1,subQ0,sQuery(id+"F6.wireOp",EDGE,"E18.3.0.0")])],"isStart":true}),makeQuery(id+"F7.opExtrude","CAP_FACE",FACE,{"disambiguationData":[OSD([subQ1,subQ0,sQuery(id+"F6.wireOp",EDGE,"E18.4.0.0")])],"isStart":true}),makeQuery(id+"F7.opExtrude","CAP_FACE",FACE,{"disambiguationData":[OSD([subQ1,subQ0,sQuery(id+"F6.wireOp",EDGE,"E18.5.0.0")])],"isStart":true}),makeQuery(id+"F7.opExtrude","CAP_FACE",FACE,{"disambiguationData":[OSD([subQ1,subQ0,sQuery(id+"F6.wireOp",EDGE,"E18.6.0.0")])],"isStart":true}),makeQuery(id+"F7.opExtrude","CAP_FACE",FACE,{"disambiguationData":[OSD([subQ1,subQ0,sQuery(id+"F6.wireOp",EDGE,"E18.7.0.0")])],"isStart":true})]}),makeQuery(id+"F31.opExtrude","SWEPT_FACE",FACE,{"disambiguationData":[OSD([sQuery(id+"F30.wireOp",EDGE,"E88")])]}),makeQuery(id+"F31.opExtrude","SWEPT_FACE",FACE,{"disambiguationData":[OSD([sQuery(id+"F30.wireOp",EDGE,"E89")])]}),makeQuery(id+"F31.opExtrude","SWEPT_FACE",FACE,{"disambiguationData":[OSD([sQuery(id+"F30.wireOp",EDGE,"E90")])]}),makeQuery(id+"F31.opExtrude","SWEPT_FACE",FACE,{"disambiguationData":[OSD([sQuery(id+"F30.wireOp",EDGE,"E94")])]})]})],"blendedInto":[makeQuery(id+"F31.boolean.opBoolean","MERGE",FACE,{"derivedFrom":[makeQuery(id+"F7.boolean.opBoolean","MERGE",FACE,{"derivedFrom":[makeQuery(id+"F5.boolean.opBoolean","MERGE",FACE,{"derivedFrom":[makeQuery(id+"F3.opExtrude","SWEPT_FACE",FACE,{"disambiguationData":[OSD([subQ1,subQ0])]}),makeQuery(id+"F5.opExtrude","SWEPT_FACE",FACE,{"disambiguationData":[OSD([sQuery(id+"F4.wireOp",EDGE,"E9")])]}),makeQuery(id+"F5.opExtrude","SWEPT_FACE",FACE,{"disambiguationData":[OSD([sQuery(id+"F4.wireOp",EDGE,"E11.MirrorCS")])]})]}),makeQuery(id+"F7.opExtrude","CAP_FACE",FACE,{"disambiguationData":[OSD([sQuery(id+"F6.wireOp",EDGE,"E16"),sQuery(id+"F6.wireOp",EDGE,"E17")])],"isStart":true}),makeQuery(id+"F7.opExtrude","CAP_FACE",FACE,{"disambiguationData":[OSD([subQ1,subQ0,sQuery(id+"F6.wireOp",EDGE,"E18.1.0.0")])],"isStart":true}),makeQuery(id+"F7.opExtrude","CAP_FACE",FACE,{"disambiguationData":[OSD([subQ1,subQ0,sQuery(id+"F6.wireOp",EDGE,"E18.2.0.0")])],"isStart":true}),makeQuery(id+"F7.opExtrude","CAP_FACE",FACE,{"disambiguationData":[OSD([subQ1,subQ0,sQuery(id+"F6.wireOp",EDGE,"E18.3.0.0")])],"isStart":true}),makeQuery(id+"F7.opExtrude","CAP_FACE",FACE,{"disambiguationData":[OSD([subQ1,subQ0,sQuery(id+"F6.wireOp",EDGE,"E18.4.0.0")])],"isStart":true}),makeQuery(id+"F7.opExtrude","CAP_FACE",FACE,{"disambiguationData":[OSD([subQ1,subQ0,sQuery(id+"F6.wireOp",EDGE,"E18.5.0.0")])],"isStart":true}),makeQuery(id+"F7.opExtrude","CAP_FACE",FACE,{"disambiguationData":[OSD([subQ1,subQ0,sQuery(id+"F6.wireOp",EDGE,"E18.6.0.0")])],"isStart":true}),makeQuery(id+"F7.opExtrude","CAP_FACE",FACE,{"disambiguationData":[OSD([subQ1,subQ0,sQuery(id+"F6.wireOp",EDGE,"E18.7.0.0")])],"isStart":true})]}),makeQuery(id+"F31.opExtrude","SWEPT_FACE",FACE,{"disambiguationData":[OSD([sQuery(id+"F30.wireOp",EDGE,"E88")])]}),makeQuery(id+"F31.opExtrude","SWEPT_FACE",FACE,{"disambiguationData":[OSD([sQuery(id+"F30.wireOp",EDGE,"E89")])]}),makeQuery(id+"F31.opExtrude","SWEPT_FACE",FACE,{"disambiguationData":[OSD([sQuery(id+"F30.wireOp",EDGE,"E90")])]}),makeQuery(id+"F31.opExtrude","SWEPT_FACE",FACE,{"disambiguationData":[OSD([sQuery(id+"F30.wireOp",EDGE,"E94")])]})]})]});}
            var Q27;
            Q27=makeQuery(id+"F31.opExtrude","CAP_EDGE",EDGE,{"disambiguationData":[OSD([sQuery(id+"F30.wireOp",EDGE,"E90")])],"isStart":false});
            var Q28;
            Q28=makeQuery(id+"F31.opExtrude","CAP_EDGE",EDGE,{"disambiguationData":[OSD([sQuery(id+"F30.wireOp",EDGE,"E94")])],"isStart":false});
            chamfer(context, id + "F36", {"entities" : qUnion([Q0, Q1, Q2, Q3, Q4, Q5, Q6, Q7, Q8, Q9, Q10, Q11, Q12, Q13, Q14, Q15, Q16, Q17, Q18, Q19, Q20, Q21, Q22, Q23, Q24, Q25, Q26, Q27, Q28]), "width" : 1 * mm, "tangentPropagation" : true});
        }
        {
            var Q0;
            Q0=makeQuery(id+"F5.opExtrude","SWEPT_EDGE",EDGE,{"disambiguationData":[OSD([sQuery(id+"F4.wireOp",EDGE,"E8"),sQuery(id+"F4.wireOp",EDGE,"E14")])]});
            var Q1;
            Q1=makeQuery(id+"F5.opExtrude","SWEPT_EDGE",EDGE,{"disambiguationData":[OSD([sQuery(id+"F4.wireOp",EDGE,"E10.MirrorCS"),sQuery(id+"F4.wireOp",EDGE,"E14")])]});
            fillet(context, id + "F37", {"entities" : qUnion([Q0, Q1]), "radius" : 5 * mm, "tangentPropagation" : true, "allowEdgeOverflow" : false});
        }
    });
